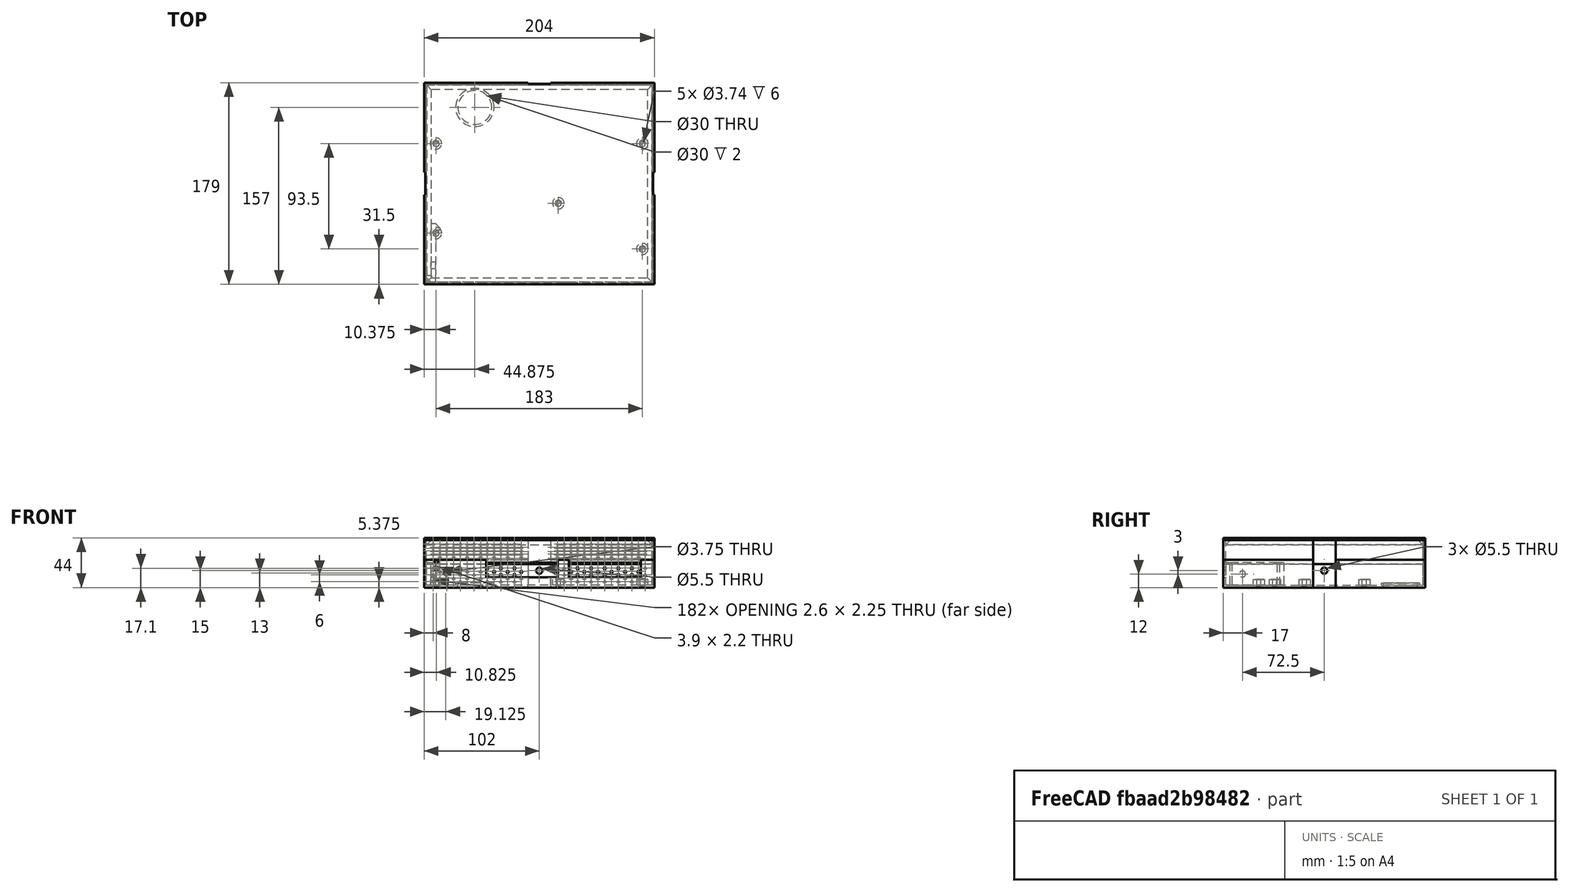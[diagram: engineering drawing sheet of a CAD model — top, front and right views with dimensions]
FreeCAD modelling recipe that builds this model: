
FCSTD DOCUMENT  (FreeCAD 2023.131R26244 +5365 (Git))
Label: Switch
License: All rights reserved
LicenseURL: http://en.wikipedia.org/wiki/All_rights_reserved
objects: Sketcher::SketchObject×26, PartDesign::Pad×13, PartDesign::Pocket×13, PartDesign::Body×4, PartDesign::LinearPattern×3, Spreadsheet::Sheet×1, PartDesign::Fillet×1, PartDesign::Chamfer×1
note: 149 computed .brp shape members not serialized (recipe doc carries the construction recipe); baked Part::Feature solids carry a one-line shape summary decoded from their .brp

FEATURE [Spreadsheet::Sheet] Spreadsheet  label="Parameters"
  PythonMode = false
  ShowCells = 0
  TreeRank = 1
  cells = A1=General; A2=Wall Thickness; B2(Thickness)=2; A3=Width; B3(Width)=200; A4=Depth; B4(Depth)=175; A6=Locking Leaver; B6=This can't be printed; A7=Thickness Multiplier; B7(Locking_Thickness_Multiplier)=2; A8=Lever Width; B8(Locking_Width)=20; A9=Lever Height; B9(Locking_Height)=40; C9=This is the distance between the horizontal locking surfaces, not the entire length of the lever.; A10=Screw Hole Offset; B10(Locking_Hole_Offset)=15; A11=Screw Hole Diameter; B11(Locking_Hole_Diameter)=5.5; A14=Switch Bottom; B14=The origin is the front-left corner, where the reset switch is.; A15=Height; B15(Switch_Bottom_Height)==2 * Switch_LED_Height + Switch_LED_Spacing + Switch_LED_Y; A16=Standoff Mount Height; B16(Switch_Mount_Height)=5.25; A17=Standoff Mount Diameter; B17(Switch_Mount_Diameter)=10.15; A18=Standoff Hole Diameter; B18(Switch_Mount_Hole_Diameter)=3; A19=M3 Nut Diameter; B19(M3_Nut_Diameter)=6.15; A20=M3 Nut Thickness; B20(M3_Nut_Thickness)=2.35; A21=M3 Insert Diameter; B21(M3_Insert_Diameter)=3.74; A22=M3 Insert Length; B22(M3_Insert_Length)=6; A23=Standoff Anchor Type; B23(Switch_Mount_Type)=insert; C23=insert or nut; A24=Mount Offset; B24(Switch_X_Offset)==(Width - 194.25) / 2; C24(Switch_Y_Offset)=0; A25=Front Right Mount; B25(Switch_FR_X)==188.5 + Switch_X_Offset; C25(Switch_FR_Y)==29.5 + Switch_Y_Offset; A26=Front Left Mount; B26(Switch_FL_X)==5.5 + Switch_X_Offset; C26(Switch_FL_Y)==43.5 + Switch_Y_Offset; A27=Middle Mount; B27(Switch_M_X)==114 + Switch_X_Offset; C27(Switch_M_Y)==70 + Switch_Y_Offset; A28=Back Right Mount; B28(Switch_BR_X)==188.5 + Switch_X_Offset; C28(Switch_BR_Y)==123 + Switch_Y_Offset; A29=Back Left Mount; B29(Switch_BL_X)==5.5 + Switch_X_Offset; C29(Switch_BL_Y)==123 + Switch_Y_Offset; A30=RJ45 Block Width; B30(RJ45_Block_Width)=63.55; A31=RJ45 Block Height; B31(RJ45_Block_Height)=13.25; A32=RJ45 Block Spacing; B32(RJ45_Block_Spacing)=10; A33=RJ45 Block Offset; B33(RJ45_Block_X)==50 + Switch_X_Offset; C33(RJ45_Block_Y)==Switch_Mount_Height + 1.75; E33==Switch_Bottom_Height - RJ45_Block_Y - RJ45_Block_Height; A34=Reset Button Diameter; B34(Switch_Reset_Diameter)=3.75; A35=Reset Button Offset; B35(Switch_Reset_X)==14.25 + Switch_X_Offset; C35(Switch_Reset_Y)==Switch_Mount_Height + 5.75; A36=Pass-through Hole Diameter; B36(Switch_Passthrough_Diameter)=30; A37=Pass-through Offset; B37(Switch_Passthrough_X)==40 + Switch_X_Offset; C37(Switch_Passthrough_Y)==155 + Switch_Y_Offset; A38=LED Width; B38(Switch_LED_Width)=3.9; A39=LED Height; B39(Switch_LED_Height)=2.2; A40=LED Spacing; B40(Switch_LED_Spacing)=4.4; A41=LED Offset; B41(Switch_LED_X)==4 + Switch_X_Offset; C41(Switch_LED_Y)==Switch_Mount_Height + 8.75; A42=Air Hole Diameter; B42(Switch_Air_Hole_Diameter)=3; A44=Switch Top; A45=Height; B45(Switch_Top_Height)==40 - Switch_Bottom_Height
FEATURE [Sketcher::SketchObject] Sketch004
  ArcFitTolerance = 1e-06
  AttachmentSupport = -> [XY_Plane001]
  ExternalBSplineMaxDegree = 5
  ExternalBSplineTolerance = 0.0001
  FullyConstrained = true
  InternalTolerance = 1e-06
  InvalidShape = false
  MakeInternals = false
  MapMode = 5
  Support = -> [XY_Plane001]
  TreeRank = 31
  ValidateShape = true
  expr: Constraints[10] = <<Parameters>>.Thickness * <<Parameters>>.Locking_Thickness_Multiplier
  expr: Constraints[11] = <<Parameters>>.Thickness * <<Parameters>>.Locking_Thickness_Multiplier / 2
  expr: Constraints[12] = <<Parameters>>.Thickness * <<Parameters>>.Locking_Thickness_Multiplier
  expr: Constraints[13] = <<Parameters>>.Thickness * <<Parameters>>.Locking_Thickness_Multiplier * 1.5
  expr: Constraints[14] = <<Parameters>>.Thickness * <<Parameters>>.Locking_Thickness_Multiplier
  expr: Constraints[15] = <<Parameters>>.Thickness * <<Parameters>>.Locking_Thickness_Multiplier
  expr: Constraints[33] = <<Parameters>>.Locking_Height
  sketch-geometry (12):
    g0: LineSegment StartX=0 StartY=4 StartZ=0 EndX=4 EndY=0 EndZ=0
    g1: LineSegment StartX=4 StartY=0 StartZ=0 EndX=8 EndY=0 EndZ=0
    g2: LineSegment StartX=8 StartY=0 StartZ=0 EndX=8 EndY=6 EndZ=0
    g3: LineSegment StartX=0 StartY=4 StartZ=0 EndX=0 EndY=6 EndZ=0
    g4: LineSegment StartX=0 StartY=6 StartZ=0 EndX=4 EndY=6 EndZ=0
    g5: LineSegment StartX=4 StartY=46 StartZ=0 EndX=4 EndY=52 EndZ=0
    g6: LineSegment StartX=4 StartY=52 StartZ=0 EndX=8 EndY=52 EndZ=0
    g7: LineSegment StartX=8 StartY=52 StartZ=0 EndX=12 EndY=48 EndZ=0
    g8: LineSegment StartX=12 StartY=48 StartZ=0 EndX=12 EndY=46 EndZ=0
    g9: LineSegment StartX=12 StartY=46 StartZ=0 EndX=8 EndY=46 EndZ=0
    g10: LineSegment StartX=4 StartY=46 StartZ=0 EndX=4 EndY=6 EndZ=0
    g11: LineSegment StartX=8 StartY=46 StartZ=0 EndX=8 EndY=6 EndZ=0
  constraints (36):
    c: PointOnObject(g0,g-2)
    c: PointOnObject(g0,g-1)
    c: Coincident(g1,g0)
    c: PointOnObject(g1,g-1)
    c: Coincident(g2,g1)
    c: Vertical(g2)
    c: Coincident(g3,g0)
    c: PointOnObject(g3,g-2)
    c: Coincident(g4,g3)
    c: Horizontal(g4)
    c: DistanceX(g0,g1) = 4
    c: DistanceY(g0,g3) = 2
    c: DistanceY(g-1,g0) = 4
    c: DistanceY(g-1,g2) = 6
    c: DistanceX(g-1,g0) = 4
    c: DistanceX(g3,g4) = 4
    c: Horizontal(g6)
    c: Coincident(g7,g6)
    c: Coincident(g8,g7)
    c: Vertical(g8)
    c: Coincident(g9,g8)
    c: Horizontal(g9)
    c: Coincident(g6,g5)
    c: Equal(g1,g6)
    c: Equal(g2,g5)
    c: Equal(g0,g7)
    c: Equal(g3,g8)
    c: Equal(g4,g9)
    c: Coincident(g10,g5)
    c: Coincident(g10,g4)
    c: Coincident(g11,g9)
    c: Coincident(g11,g2)
    c: Parallel(g0,g7)
    c: DistanceY(g3,g8) = 40
    c: Vertical(g10)
    c: Vertical(g11)
FEATURE [PartDesign::Pad] Pad003
  AddSubType = 0
  AlongSketchNormal = false
  AutoTaperInnerAngle = true
  CheckUpToFaceLimits = true
  ClaimChildren = false
  Direction = (0,0,1)
  Fit = 0
  FitJoin = 0
  InnerFit = 0
  InnerFitJoin = 0
  InvalidShape = false
  Length = 20
  Length2 = 100
  Linearize = true
  NewSolid = false
  Profile = -> Sketch004
  Suppress = false
  TaperInnerAngle = 0
  TaperInnerAngleRev = 0
  TreeRank = 32
  Type = 0
  ValidateShape = true
  _ProfileBasedVersion = 1
  expr: Length = <<Parameters>>.Locking_Width
FEATURE [Sketcher::SketchObject] Sketch005  label="Bottom Sketch"
  ArcFitTolerance = 1e-06
  AttachmentSupport = -> [XY_Plane]
  ExternalBSplineMaxDegree = 5
  ExternalBSplineTolerance = 0.0001
  FullyConstrained = true
  InternalTolerance = 1e-06
  InvalidShape = false
  MakeInternals = false
  MapMode = 5
  Support = -> [XY_Plane]
  TreeRank = 45
  ValidateShape = true
  expr: Constraints[10] = <<Parameters>>.Width + 2 * <<Parameters>>.Thickness
  expr: Constraints[11] = <<Parameters>>.Depth + 2 * <<Parameters>>.Thickness
  expr: Constraints[12] = <<Parameters>>.Switch_Passthrough_Diameter
  expr: Constraints[13] = <<Parameters>>.Switch_Passthrough_X
  expr: Constraints[14] = <<Parameters>>.Switch_Passthrough_Y
  expr: Constraints[8] = <<Parameters>>.Thickness
  expr: Constraints[9] = <<Parameters>>.Thickness
  sketch-geometry (5):
    g0: LineSegment StartX=-2 StartY=-2 StartZ=0 EndX=202 EndY=-2 EndZ=0
    g1: LineSegment StartX=202 StartY=-2 StartZ=0 EndX=202 EndY=177 EndZ=0
    g2: LineSegment StartX=202 StartY=177 StartZ=0 EndX=-2 EndY=177 EndZ=0
    g3: LineSegment StartX=-2 StartY=177 StartZ=0 EndX=-2 EndY=-2 EndZ=0
    g4: Circle CenterX=42.875 CenterY=155 CenterZ=0 NormalX=0 NormalY=0 NormalZ=1 AngleXU=0 Radius=15
  constraints (15):
    c: Coincident(g0,g1)
    c: Coincident(g1,g2)
    c: Coincident(g2,g3)
    c: Coincident(g3,g0)
    c: Horizontal(g0)
    c: Horizontal(g2)
    c: Vertical(g1)
    c: Vertical(g3)
    c: DistanceX(g0,g-1) = 2
    c: DistanceY(g0,g-1) = 2
    c: DistanceX(g0,g0) = 204
    c: DistanceY(g0,g2) = 179
    c: Diameter(g4) = 30
    c: DistanceX(g-1,g4) = 42.875
    c: DistanceY(g-1,g4) = 155
FEATURE [PartDesign::Pad] Pad  label="Bottom"
  AddSubType = 0
  AlongSketchNormal = false
  AutoTaperInnerAngle = true
  CheckUpToFaceLimits = true
  ClaimChildren = false
  Direction = (0,0,1)
  Fit = 0
  FitJoin = 0
  InnerFit = 0
  InnerFitJoin = 0
  InvalidShape = false
  Length = 2
  Length2 = 100
  Linearize = true
  NewSolid = false
  Profile = -> Sketch005
  Reversed = true
  Suppress = false
  TaperInnerAngle = 0
  TaperInnerAngleRev = 0
  TreeRank = 46
  Type = 0
  ValidateShape = true
  _ProfileBasedVersion = 1
  expr: Length = <<Parameters>>.Thickness
FEATURE [Sketcher::SketchObject] Sketch006  label="Standoff Mounts Drawing"
  ArcFitTolerance = 1e-06
  AttachmentSupport = -> [Pad]
  ExternalBSplineMaxDegree = 5
  ExternalBSplineTolerance = 0.0001
  FullyConstrained = true
  InternalTolerance = 1e-06
  InvalidShape = false
  MakeInternals = false
  MapMode = 5
  Support = -> [Pad]
  TreeRank = 47
  ValidateShape = true
  expr: Constraints[0] = <<Parameters>>.Switch_Mount_Diameter
  expr: Constraints[11] = <<Parameters>>.Switch_BR_X
  expr: Constraints[12] = <<Parameters>>.Switch_BR_Y
  expr: Constraints[13] = <<Parameters>>.Switch_BL_X
  expr: Constraints[14] = <<Parameters>>.Switch_BL_Y
  expr: Constraints[16] = <<Parameters>>.Switch_Mount_Hole_Diameter
  expr: Constraints[1] = <<Parameters>>.Switch_FR_X
  expr: Constraints[2] = <<Parameters>>.Switch_FR_Y
  expr: Constraints[4] = <<Parameters>>.Switch_FL_Y
  expr: Constraints[5] = <<Parameters>>.Switch_FL_X
  expr: Constraints[7] = <<Parameters>>.Switch_M_X
  expr: Constraints[8] = <<Parameters>>.Switch_M_Y
  sketch-geometry (10):
    g0: Circle CenterX=191.375 CenterY=29.5 CenterZ=0 NormalX=0 NormalY=0 NormalZ=1 AngleXU=0 Radius=5.075
    g1: Circle CenterX=8.375 CenterY=43.5 CenterZ=0 NormalX=0 NormalY=0 NormalZ=1 AngleXU=0 Radius=5.075
    g2: Circle CenterX=116.875 CenterY=70 CenterZ=0 NormalX=0 NormalY=0 NormalZ=1 AngleXU=0 Radius=5.075
    g3: Circle CenterX=191.375 CenterY=123 CenterZ=0 NormalX=0 NormalY=0 NormalZ=1 AngleXU=0 Radius=5.075
    g4: Circle CenterX=8.375 CenterY=123 CenterZ=0 NormalX=0 NormalY=0 NormalZ=1 AngleXU=0 Radius=5.075
    g5: Circle CenterX=191.375 CenterY=29.5 CenterZ=0 NormalX=0 NormalY=0 NormalZ=1 AngleXU=0 Radius=1.5
    g6: Circle CenterX=116.875 CenterY=70 CenterZ=0 NormalX=0 NormalY=0 NormalZ=1 AngleXU=0 Radius=1.5
    g7: Circle CenterX=191.375 CenterY=123 CenterZ=0 NormalX=0 NormalY=0 NormalZ=1 AngleXU=0 Radius=1.5
    g8: Circle CenterX=8.375 CenterY=43.5 CenterZ=0 NormalX=0 NormalY=0 NormalZ=1 AngleXU=0 Radius=1.5
    g9: Circle CenterX=8.375 CenterY=123 CenterZ=0 NormalX=0 NormalY=0 NormalZ=1 AngleXU=0 Radius=1.5
  constraints (25):
    c: Diameter(g0) = 10.15
    c: DistanceX(g-1,g0) = 191.375
    c: DistanceY(g-1,g0) = 29.5
    c: Equal(g0,g1)
    c: DistanceY(g-1,g1) = 43.5
    c: DistanceX(g-1,g1) = 8.375
    c: Equal(g0,g2)
    c: DistanceX(g-1,g2) = 116.875
    c: DistanceY(g-1,g2) = 70
    c: Equal(g0,g3)
    c: Equal(g0,g4)
    c: DistanceX(g-1,g3) = 191.375
    c: DistanceY(g-1,g3) = 123
    c: DistanceX(g-1,g4) = 8.375
    c: DistanceY(g-1,g4) = 123
    c: Coincident(g5,g0)
    c: Diameter(g5) = 3
    c: Coincident(g6,g2)
    c: Coincident(g7,g3)
    c: Coincident(g8,g1)
    c: Coincident(g9,g4)
    c: Equal(g5,g6)
    c: Equal(g5,g8)
    c: Equal(g5,g7)
    c: Equal(g5,g9)
FEATURE [PartDesign::Pad] Pad004  label="Standoff Mounts"
  AddSubType = 0
  AlongSketchNormal = false
  AutoTaperInnerAngle = true
  BaseFeature = -> Pad
  CheckUpToFaceLimits = true
  ClaimChildren = false
  Direction = (0,0,1)
  Fit = 0
  FitJoin = 0
  InnerFit = 0
  InnerFitJoin = 0
  InvalidShape = false
  Length = 5.25
  Length2 = 100
  Linearize = true
  NewSolid = false
  Profile = -> Sketch006
  Suppress = false
  TaperInnerAngle = 0
  TaperInnerAngleRev = 0
  TreeRank = 48
  Type = 0
  ValidateShape = true
  _ProfileBasedVersion = 1
  expr: Length = <<Parameters>>.Switch_Mount_Height
FEATURE [Sketcher::SketchObject] Sketch007  label="Nut Holes Sketch"
  ArcFitTolerance = 1e-06
  AttachmentSupport = -> [Pad004]
  ExternalBSplineMaxDegree = 5
  ExternalBSplineTolerance = 0.0001
  FullyConstrained = false
  InternalTolerance = 1e-06
  InvalidShape = false
  MakeInternals = false
  MapMode = 5
  Placement = pos=(0,0,5.25) rot=(0,0,1;0rad)
  Support = -> [Pad004]
  TreeRank = 49
  ValidateShape = true
  expr: Constraints[17] = <<Parameters>>.M3_Nut_Diameter
  expr: Constraints[18] = <<Parameters>>.Switch_FR_X
  expr: Constraints[19] = <<Parameters>>.Switch_FR_Y
  expr: Constraints[74] = <<Parameters>>.Switch_M_X
  expr: Constraints[75] = <<Parameters>>.Switch_M_Y
  expr: Constraints[76] = <<Parameters>>.Switch_FL_X
  expr: Constraints[77] = <<Parameters>>.Switch_FL_Y
  expr: Constraints[78] = <<Parameters>>.Switch_BL_X
  expr: Constraints[79] = <<Parameters>>.Switch_BL_Y
  expr: Constraints[98] = <<Parameters>>.Switch_BR_X
  expr: Constraints[99] = <<Parameters>>.Switch_BR_Y
  sketch-geometry (35):
    g0: LineSegment StartX=188.799 StartY=31.1785 StartZ=0 EndX=188.633 EndY=28.108 EndZ=0
    g1: LineSegment StartX=188.633 StartY=28.108 StartZ=0 EndX=191.21 EndY=26.4295 EndZ=0
    g2: LineSegment StartX=191.21 StartY=26.4295 StartZ=0 EndX=193.951 EndY=27.8215 EndZ=0
    g3: LineSegment StartX=193.951 StartY=27.8215 StartZ=0 EndX=194.117 EndY=30.892 EndZ=0
    g4: LineSegment StartX=194.117 StartY=30.892 StartZ=0 EndX=191.54 EndY=32.5705 EndZ=0
    g5: LineSegment StartX=191.54 StartY=32.5705 StartZ=0 EndX=188.799 EndY=31.1785 EndZ=0
    g6: Circle [constr] CenterX=191.375 CenterY=29.5 CenterZ=0 NormalX=0 NormalY=0 NormalZ=1 AngleXU=0 Radius=3.075
    g7: LineSegment StartX=117.133 StartY=73.0641 StartZ=0 EndX=114.351 EndY=71.7559 EndZ=0
    g8: LineSegment StartX=114.351 StartY=71.7559 StartZ=0 EndX=114.092 EndY=68.6917 EndZ=0
    g9: LineSegment StartX=114.092 StartY=68.6917 StartZ=0 EndX=116.617 EndY=66.9359 EndZ=0
    g10: LineSegment StartX=116.617 StartY=66.9359 StartZ=0 EndX=119.399 EndY=68.2441 EndZ=0
    g11: LineSegment StartX=119.399 StartY=68.2441 StartZ=0 EndX=119.658 EndY=71.3083 EndZ=0
    g12: LineSegment StartX=119.658 StartY=71.3083 StartZ=0 EndX=117.133 EndY=73.0641 EndZ=0
    g13: Circle [constr] CenterX=116.875 CenterY=70 CenterZ=0 NormalX=0 NormalY=0 NormalZ=1 AngleXU=0 Radius=3.075
    g14: LineSegment StartX=10.9135 StartY=45.2354 StartZ=0 EndX=8.14135 EndY=46.5661 EndZ=0
    g15: LineSegment StartX=8.14135 StartY=46.5661 StartZ=0 EndX=5.60285 EndY=44.8307 EndZ=0
    g16: LineSegment StartX=5.60285 StartY=44.8307 StartZ=0 EndX=5.83649 EndY=41.7646 EndZ=0
    g17: LineSegment StartX=5.83649 StartY=41.7646 StartZ=0 EndX=8.60865 EndY=40.4339 EndZ=0
    g18: LineSegment StartX=8.60865 StartY=40.4339 StartZ=0 EndX=11.1472 EndY=42.1693 EndZ=0
    g19: LineSegment StartX=11.1472 StartY=42.1693 StartZ=0 EndX=10.9135 EndY=45.2354 EndZ=0
    g20: Circle [constr] CenterX=8.375 CenterY=43.5 CenterZ=0 NormalX=0 NormalY=0 NormalZ=1 AngleXU=0 Radius=3.075
    g21: LineSegment StartX=10.8456 StartY=124.831 StartZ=0 EndX=8.0248 EndY=126.055 EndZ=0
    g22: LineSegment StartX=8.0248 StartY=126.055 StartZ=0 EndX=5.5542 EndY=124.224 EndZ=0
    g23: LineSegment StartX=5.5542 StartY=124.224 StartZ=0 EndX=5.9044 EndY=121.169 EndZ=0
    g24: LineSegment StartX=5.9044 StartY=121.169 StartZ=0 EndX=8.7252 EndY=119.945 EndZ=0
    g25: LineSegment StartX=8.7252 StartY=119.945 StartZ=0 EndX=11.1958 EndY=121.776 EndZ=0
    g26: LineSegment StartX=11.1958 StartY=121.776 StartZ=0 EndX=10.8456 EndY=124.831 EndZ=0
    g27: Circle [constr] CenterX=8.375 CenterY=123 CenterZ=0 NormalX=0 NormalY=0 NormalZ=1 AngleXU=0 Radius=3.075
    g28: LineSegment StartX=188.744 StartY=124.591 StartZ=0 EndX=188.681 EndY=121.517 EndZ=0
    g29: LineSegment StartX=188.681 StartY=121.517 StartZ=0 EndX=191.313 EndY=119.926 EndZ=0
    g30: LineSegment StartX=191.313 StartY=119.926 StartZ=0 EndX=194.006 EndY=121.409 EndZ=0
    g31: LineSegment StartX=194.006 StartY=121.409 StartZ=0 EndX=194.069 EndY=124.483 EndZ=0
    g32: LineSegment StartX=194.069 StartY=124.483 StartZ=0 EndX=191.437 EndY=126.074 EndZ=0
    g33: LineSegment StartX=191.437 StartY=126.074 StartZ=0 EndX=188.744 EndY=124.591 EndZ=0
    g34: Circle [constr] CenterX=191.375 CenterY=123 CenterZ=0 NormalX=0 NormalY=0 NormalZ=1 AngleXU=0 Radius=3.075
  constraints (80):
    c: Coincident(g0,g1)
    c: Coincident(g1,g2)
    c: Coincident(g2,g3)
    c: Coincident(g3,g4)
    c: Coincident(g4,g5)
    c: Coincident(g5,g0)
    c: Equal(g0, g1-g5) x5
    c: PointOnObject(g0,g6)
    c: PointOnObject(g1,g6)
    c: PointOnObject(g2,g6)
    c: PointOnObject(g3,g6)
    c: PointOnObject(g4,g6)
    c: PointOnObject(g5,g6)
    c: Diameter(g6) = 6.15
    c: DistanceX(g-1,g6) = 191.375
    c: DistanceY(g-1,g6) = 29.5
    c: Coincident(g7,g8)
    c: Coincident(g8,g9)
    c: Coincident(g9,g10)
    c: Coincident(g10,g11)
    c: Coincident(g11,g12)
    c: Coincident(g12,g7)
    c: Equal(g7, g8-g12) x5
    c: PointOnObject(g7,g13)
    c: PointOnObject(g8,g13)
    c: PointOnObject(g9,g13)
    c: PointOnObject(g10,g13)
    c: PointOnObject(g11,g13)
    c: PointOnObject(g12,g13)
    c: Coincident(g14,g15)
    c: Coincident(g15,g16)
    c: Coincident(g16,g17)
    c: Coincident(g17,g18)
    c: Coincident(g18,g19)
    c: Coincident(g19,g14)
    c: Equal(g14, g15-g19) x5
    c: PointOnObject(g14,g20)
    c: PointOnObject(g15,g20)
    c: PointOnObject(g16,g20)
    c: PointOnObject(g17,g20)
    c: PointOnObject(g18,g20)
    c: PointOnObject(g19,g20)
    c: Coincident(g21,g22)
    c: Coincident(g22,g23)
    c: Coincident(g23,g24)
    c: Coincident(g24,g25)
    c: Coincident(g25,g26)
    c: Coincident(g26,g21)
    c: Equal(g21, g22-g26) x5
    c: PointOnObject(g21,g27)
    c: PointOnObject(g22,g27)
    c: PointOnObject(g23,g27)
    c: PointOnObject(g24,g27)
    c: PointOnObject(g25,g27)
    c: PointOnObject(g26,g27)
    c: Equal(g6,g13)
    c: Equal(g6,g20)
    c: Equal(g6,g27)
    c: DistanceX(g-1,g13) = 116.875
    c: DistanceY(g-1,g13) = 70
    c: DistanceX(g-1,g20) = 8.375
    c: DistanceY(g-1,g20) = 43.5
    c: DistanceX(g-1,g27) = 8.375
    c: DistanceY(g-1,g27) = 123
    c: Coincident(g28,g29)
    c: Coincident(g29,g30)
    c: Coincident(g30,g31)
    c: Coincident(g31,g32)
    c: Coincident(g32,g33)
    c: Coincident(g33,g28)
    c: Equal(g28, g29-g33) x5
    c: PointOnObject(g28,g34)
    c: PointOnObject(g29,g34)
    c: PointOnObject(g30,g34)
    c: PointOnObject(g31,g34)
    c: PointOnObject(g32,g34)
    c: PointOnObject(g33,g34)
    c: Equal(g6,g34)
    c: DistanceX(g-1,g34) = 191.375
    c: DistanceY(g-1,g34) = 123
FEATURE [PartDesign::Pocket] Pocket  label="Nut Holes"
  AddSubType = 1
  AutoTaperInnerAngle = true
  BaseFeature = -> Pad004
  CheckUpToFaceLimits = true
  ClaimChildren = false
  Fit = 0
  FitJoin = 0
  InnerFit = 0
  InnerFitJoin = 0
  InvalidShape = false
  Length = 0.0001
  Length2 = 100
  Linearize = true
  NewSolid = false
  Profile = -> Sketch007
  Suppress = false
  TaperInnerAngle = 0
  TaperInnerAngleRev = 0
  TreeRank = 50
  Type = 0
  ValidateShape = true
  _ProfileBasedVersion = 1
  _Version = 1
  expr: Length = <<Parameters>>.Switch_Mount_Type == <<nut>> ? <<Parameters>>.M3_Nut_Thickness : 0.0001
FEATURE [Sketcher::SketchObject] Sketch008  label="Walls Sketch"
  ArcFitTolerance = 1e-06
  AttachmentSupport = -> [Pocket]
  ExternalBSplineMaxDegree = 5
  ExternalBSplineTolerance = 0.0001
  FullyConstrained = true
  InternalTolerance = 1e-06
  InvalidShape = false
  MakeInternals = false
  MapMode = 5
  Support = -> [Pocket]
  TreeRank = 51
  ValidateShape = true
  expr: Constraints[10] = <<Parameters>>.Width + 2 * <<Parameters>>.Thickness
  expr: Constraints[11] = <<Parameters>>.Depth + 2 * <<Parameters>>.Thickness
  expr: Constraints[20] = <<Parameters>>.Thickness
  expr: Constraints[21] = <<Parameters>>.Thickness
  expr: Constraints[22] = <<Parameters>>.Width
  expr: Constraints[23] = <<Parameters>>.Depth
  expr: Constraints[8] = <<Parameters>>.Thickness
  expr: Constraints[9] = <<Parameters>>.Thickness
  sketch-geometry (8):
    g0: LineSegment StartX=-2 StartY=-2 StartZ=0 EndX=202 EndY=-2 EndZ=0
    g1: LineSegment StartX=202 StartY=-2 StartZ=0 EndX=202 EndY=177 EndZ=0
    g2: LineSegment StartX=202 StartY=177 StartZ=0 EndX=-2 EndY=177 EndZ=0
    g3: LineSegment StartX=-2 StartY=177 StartZ=0 EndX=-2 EndY=-2 EndZ=0
    g4: LineSegment StartX=1e-16 StartY=175 StartZ=0 EndX=200 EndY=175 EndZ=0
    g5: LineSegment StartX=200 StartY=175 StartZ=0 EndX=200 EndY=0 EndZ=0
    g6: LineSegment StartX=200 StartY=1e-16 StartZ=0 EndX=0 EndY=1e-16 EndZ=0
    g7: LineSegment StartX=1e-16 StartY=1e-16 StartZ=0 EndX=1e-16 EndY=175 EndZ=0
  constraints (24):
    c: Coincident(g0,g1)
    c: Coincident(g1,g2)
    c: Coincident(g2,g3)
    c: Coincident(g3,g0)
    c: Horizontal(g0)
    c: Horizontal(g2)
    c: Vertical(g1)
    c: Vertical(g3)
    c: DistanceY(g0,g-1) = 2
    c: DistanceX(g0,g-1) = 2
    c: DistanceX(g0,g0) = 204
    c: DistanceY(g0,g2) = 179
    c: Coincident(g4,g5)
    c: Coincident(g5,g6)
    c: Coincident(g6,g7)
    c: Coincident(g7,g4)
    c: Horizontal(g4)
    c: Horizontal(g6)
    c: Vertical(g5)
    c: Vertical(g7)
    c: DistanceX(g0,g6) = 2
    c: DistanceY(g0,g6) = 2
    c: DistanceX(g4,g4) = 200
    c: DistanceY(g5,g4) = 175
FEATURE [Sketcher::SketchObject] Sketch011  label="Passthrough Support Sketch"
  ArcFitTolerance = 1e-06
  ExternalBSplineMaxDegree = 5
  ExternalBSplineTolerance = 0.0001
  FullyConstrained = true
  InternalTolerance = 1e-06
  InvalidShape = false
  MakeInternals = false
  MapMode = 5
  TreeRank = 57
  ValidateShape = true
  expr: Constraints[1] = <<Parameters>>.Switch_Passthrough_Diameter
  expr: Constraints[2] = <<Parameters>>.Switch_Passthrough_Diameter + 2 * <<Parameters>>.Thickness
  expr: Constraints[3] = <<Parameters>>.Switch_Passthrough_X
  expr: Constraints[4] = <<Parameters>>.Switch_Passthrough_Y
  sketch-geometry (2):
    g0: Circle CenterX=42.875 CenterY=155 CenterZ=0 NormalX=0 NormalY=0 NormalZ=1 AngleXU=0 Radius=17
    g1: Circle CenterX=42.875 CenterY=155 CenterZ=0 NormalX=0 NormalY=0 NormalZ=1 AngleXU=0 Radius=15
  constraints (5):
    c: Coincident(g1,g0)
    c: Diameter(g1) = 30
    c: Diameter(g0) = 34
    c: DistanceX(g-1,g0) = 42.875
    c: DistanceY(g-1,g0) = 155
FEATURE [Sketcher::SketchObject] Sketch
  ArcFitTolerance = 1e-06
  AttachmentSupport = -> [Pad003]
  ExternalBSplineMaxDegree = 5
  ExternalBSplineTolerance = 0.0001
  FullyConstrained = true
  InternalTolerance = 1e-06
  InvalidShape = false
  MakeInternals = false
  MapMode = 5
  Placement = pos=(4,0,0) rot=(0.57735,-0.57735,-0.57735;2.0944rad)
  Support = -> [Pad003]
  TreeRank = 62
  ValidateShape = true
  expr: Constraints[0] = <<Parameters>>.Locking_Hole_Diameter
  expr: Constraints[1] = <<Parameters>>.Locking_Width / 2
  expr: Constraints[2] = <<Parameters>>.Locking_Hole_Offset
  sketch-geometry (1):
    g0: Circle CenterX=-15 CenterY=10 CenterZ=0 NormalX=0 NormalY=0 NormalZ=1 AngleXU=0 Radius=2.75
  constraints (3):
    c: Diameter(g0) = 5.5
    c: DistanceY(g-1,g0) = 10
    c: DistanceX(g0,g-1) = 15
FEATURE [PartDesign::Pocket] Pocket004
  AddSubType = 1
  AutoTaperInnerAngle = true
  BaseFeature = -> Pad003
  CheckUpToFaceLimits = true
  ClaimChildren = false
  Fit = 0
  FitJoin = 0
  InnerFit = 0
  InnerFitJoin = 0
  InvalidShape = false
  Length = 4
  Length2 = 100
  Linearize = true
  NewSolid = false
  Profile = -> Sketch
  Suppress = false
  TaperInnerAngle = 0
  TaperInnerAngleRev = 0
  TreeRank = 63
  Type = 0
  ValidateShape = true
  _ProfileBasedVersion = 1
  _Version = 1
  expr: Length = <<Parameters>>.Locking_Thickness_Multiplier * <<Parameters>>.Thickness
FEATURE [PartDesign::Fillet] Fillet
  AddSubType = 0
  Base = -> Pocket004 [Edge3,Edge8,Edge6,Edge7,Edge2,Edge29,Edge19,Edge9,Edge28,Edge18,Edge20,Edge10]
  BaseFeature = -> Pocket004
  InvalidShape = false
  NewSolid = false
  Radius = 1
  SupportTransform = false
  Suppress = false
  TreeRank = 66
  ValidateShape = true
FEATURE [PartDesign::Body] Body001  label="Locking Lever"
  AutoGroupSolids = false
  ClaimAllChildren = false
  ExportMode = 0
  Group = -> [Sketch004,Pad003,Sketch,Pocket004,Fillet]
  InvalidShape = false
  Origin = -> Origin001
  Tip = -> Fillet
  TreeRank = 30
  ValidateShape = true
  _ExportChildren = -> [Pad003,Pocket004,Fillet]
  _GroupVersion = 1
FEATURE [Sketcher::SketchObject] Sketch018  label="Switch Top Walls Sketch"
  ArcFitTolerance = 1e-06
  AttachmentOffset = pos=(0,0,22.8) rot=(0,0,1;0rad)
  AttachmentSupport = -> [XY_Plane002]
  ExternalBSplineMaxDegree = 5
  ExternalBSplineTolerance = 0.0001
  FullyConstrained = true
  InternalTolerance = 1e-06
  InvalidShape = false
  MakeInternals = false
  MapMode = 5
  Placement = pos=(0,0,22.8) rot=(0,0,1;0rad)
  Support = -> [XY_Plane002]
  TreeRank = 88
  ValidateShape = true
  expr: AttachmentOffset.Base.z = <<Parameters>>.Switch_Bottom_Height
  expr: Constraints[10] = <<Parameters>>.Thickness
  expr: Constraints[11] = <<Parameters>>.Thickness
  expr: Constraints[20] = <<Parameters>>.Width
  expr: Constraints[21] = <<Parameters>>.Depth
  expr: Constraints[8] = <<Parameters>>.Width + 2 * <<Parameters>>.Thickness
  expr: Constraints[9] = <<Parameters>>.Depth + 2 * <<Parameters>>.Thickness
  sketch-geometry (8):
    g0: LineSegment StartX=-2 StartY=177 StartZ=0 EndX=202 EndY=177 EndZ=0
    g1: LineSegment StartX=202 StartY=177 StartZ=0 EndX=202 EndY=-2 EndZ=0
    g2: LineSegment StartX=202 StartY=-2 StartZ=0 EndX=-2 EndY=-2 EndZ=0
    g3: LineSegment StartX=-2 StartY=-2 StartZ=0 EndX=-2 EndY=177 EndZ=0
    g4: LineSegment StartX=0 StartY=175 StartZ=0 EndX=200 EndY=175 EndZ=0
    g5: LineSegment StartX=200 StartY=175 StartZ=0 EndX=200 EndY=0 EndZ=0
    g6: LineSegment StartX=200 StartY=0 StartZ=0 EndX=0 EndY=0 EndZ=0
    g7: LineSegment StartX=0 StartY=0 StartZ=0 EndX=0 EndY=175 EndZ=0
  constraints (23):
    c: Coincident(g0,g1)
    c: Coincident(g1,g2)
    c: Coincident(g2,g3)
    c: Coincident(g3,g0)
    c: Horizontal(g0)
    c: Horizontal(g2)
    c: Vertical(g1)
    c: Vertical(g3)
    c: DistanceX(g2,g1) = 204
    c: DistanceY(g2,g0) = 179
    c: DistanceY(g2,g-1) = 2
    c: DistanceX(g2,g-1) = 2
    c: Coincident(g4,g5)
    c: Coincident(g5,g6)
    c: Coincident(g6,g7)
    c: Coincident(g7,g4)
    c: Horizontal(g4)
    c: Horizontal(g6)
    c: Vertical(g5)
    c: Vertical(g7)
    c: DistanceX(g6,g5) = 200
    c: DistanceY(g6,g4) = 175
    c: Coincident(g6,g-1)
FEATURE [PartDesign::Pad] Pad007  label="Switch Top Walls"
  AddSubType = 0
  AlongSketchNormal = false
  AutoTaperInnerAngle = true
  CheckUpToFaceLimits = true
  ClaimChildren = false
  Direction = (0,0,1)
  Fit = 0
  FitJoin = 0
  InnerFit = 0
  InnerFitJoin = 0
  InvalidShape = false
  Length = 17.2
  Length2 = 100
  Linearize = true
  NewSolid = false
  Profile = -> Sketch018
  Suppress = false
  TaperInnerAngle = 0
  TaperInnerAngleRev = 0
  TreeRank = 89
  Type = 0
  ValidateShape = true
  _ProfileBasedVersion = 1
  expr: Length = <<Parameters>>.Switch_Top_Height
FEATURE [Sketcher::SketchObject] Sketch019  label="Switch Top Top Sketch"
  ArcFitTolerance = 1e-06
  AttachmentSupport = -> [Pad007]
  ExternalBSplineMaxDegree = 5
  ExternalBSplineTolerance = 0.0001
  FullyConstrained = true
  InternalTolerance = 1e-06
  InvalidShape = false
  MakeInternals = false
  MapMode = 5
  Placement = pos=(0,0,40) rot=(0,0,1;0rad)
  Support = -> [Pad007]
  TreeRank = 90
  ValidateShape = true
  expr: Constraints[10] = <<Parameters>>.Thickness
  expr: Constraints[11] = <<Parameters>>.Thickness
  expr: Constraints[8] = <<Parameters>>.Width + 2 * <<Parameters>>.Thickness
  expr: Constraints[9] = <<Parameters>>.Depth + 2 * <<Parameters>>.Thickness
  sketch-geometry (4):
    g0: LineSegment StartX=-2 StartY=177 StartZ=0 EndX=202 EndY=177 EndZ=0
    g1: LineSegment StartX=202 StartY=177 StartZ=0 EndX=202 EndY=-2 EndZ=0
    g2: LineSegment StartX=202 StartY=-2 StartZ=0 EndX=-2 EndY=-2 EndZ=0
    g3: LineSegment StartX=-2 StartY=-2 StartZ=0 EndX=-2 EndY=177 EndZ=0
  constraints (12):
    c: Coincident(g0,g1)
    c: Coincident(g1,g2)
    c: Coincident(g2,g3)
    c: Coincident(g3,g0)
    c: Horizontal(g0)
    c: Horizontal(g2)
    c: Vertical(g1)
    c: Vertical(g3)
    c: DistanceX(g2,g1) = 204
    c: DistanceY(g1,g0) = 179
    c: DistanceX(g2,g-1) = 2
    c: DistanceY(g2,g-1) = 2
FEATURE [PartDesign::Pad] Pad008  label="Switch Top Top"
  AddSubType = 0
  AlongSketchNormal = false
  AutoTaperInnerAngle = true
  BaseFeature = -> Pad007
  CheckUpToFaceLimits = true
  ClaimChildren = false
  Direction = (0,0,1)
  Fit = 0
  FitJoin = 0
  InnerFit = 0
  InnerFitJoin = 0
  InvalidShape = false
  Length = 2
  Length2 = 100
  Linearize = true
  NewSolid = false
  Profile = -> Sketch019
  Suppress = false
  TaperInnerAngle = 0
  TaperInnerAngleRev = 0
  TreeRank = 91
  Type = 0
  ValidateShape = true
  _ProfileBasedVersion = 1
  expr: Length = <<Parameters>>.Thickness
FEATURE [Sketcher::SketchObject] Sketch020  label="Switch Top Wall Recess Sketch"
  ArcFitTolerance = 1e-06
  AttachmentSupport = -> [Pad008]
  ExternalBSplineMaxDegree = 5
  ExternalBSplineTolerance = 0.0001
  FullyConstrained = true
  InternalTolerance = 1e-06
  InvalidShape = false
  MakeInternals = false
  MapMode = 5
  Placement = pos=(0,0,22.8) rot=(1,0,0;3.14159rad)
  Support = -> [Pad008]
  TreeRank = 92
  ValidateShape = true
  expr: Constraints[10] = <<Parameters>>.Thickness / 2
  expr: Constraints[11] = <<Parameters>>.Thickness / 2
  expr: Constraints[21] = <<Parameters>>.Width
  expr: Constraints[22] = <<Parameters>>.Depth
  expr: Constraints[24] = <<Parameters>>.RJ45_Block_X
  expr: Constraints[26] = <<Parameters>>.RJ45_Block_Width
  expr: Constraints[30] = <<Parameters>>.RJ45_Block_Spacing
  expr: Constraints[34] = <<Parameters>>.RJ45_Block_Width
  expr: Constraints[49] = <<Parameters>>.Switch_LED_Width
  expr: Constraints[50] = <<Parameters>>.Switch_LED_X
  expr: Constraints[8] = <<Parameters>>.Width + <<Parameters>>.Thickness
  expr: Constraints[9] = <<Parameters>>.Depth + <<Parameters>>.Thickness
  sketch-geometry (20):
    g0: LineSegment StartX=-1 StartY=1 StartZ=0 EndX=6.875 EndY=1 EndZ=0
    g1: LineSegment StartX=201 StartY=1 StartZ=0 EndX=201 EndY=-176 EndZ=0
    g2: LineSegment StartX=201 StartY=-176 StartZ=0 EndX=-1 EndY=-176 EndZ=0
    g3: LineSegment StartX=-1 StartY=-176 StartZ=0 EndX=-1 EndY=1 EndZ=0
    g4: LineSegment StartX=0 StartY=0 StartZ=0 EndX=6.875 EndY=0 EndZ=0
    g5: LineSegment StartX=200 StartY=0 StartZ=0 EndX=200 EndY=-175 EndZ=0
    g6: LineSegment StartX=200 StartY=-175 StartZ=0 EndX=0 EndY=-175 EndZ=0
    g7: LineSegment StartX=0 StartY=-175 StartZ=0 EndX=0 EndY=0 EndZ=0
    g8: LineSegment StartX=52.875 StartY=1 StartZ=0 EndX=52.875 EndY=0 EndZ=0
    g9: LineSegment StartX=116.425 StartY=1 StartZ=0 EndX=116.425 EndY=0 EndZ=0
    g10: LineSegment StartX=126.425 StartY=1 StartZ=0 EndX=126.425 EndY=0 EndZ=0
    g11: LineSegment StartX=189.975 StartY=1 StartZ=0 EndX=189.975 EndY=0 EndZ=0
    g12: LineSegment StartX=116.425 StartY=0 StartZ=0 EndX=126.425 EndY=0 EndZ=0
    g13: LineSegment StartX=116.425 StartY=1 StartZ=0 EndX=126.425 EndY=1 EndZ=0
    g14: LineSegment StartX=189.975 StartY=0 StartZ=0 EndX=200 EndY=0 EndZ=0
    g15: LineSegment StartX=189.975 StartY=1 StartZ=0 EndX=201 EndY=1 EndZ=0
    g16: LineSegment StartX=6.875 StartY=1 StartZ=0 EndX=6.875 EndY=0 EndZ=0
    g17: LineSegment StartX=10.775 StartY=1 StartZ=0 EndX=10.775 EndY=0 EndZ=0
    g18: LineSegment StartX=10.775 StartY=0 StartZ=0 EndX=52.875 EndY=0 EndZ=0
    g19: LineSegment StartX=10.775 StartY=1 StartZ=0 EndX=52.875 EndY=1 EndZ=0
  constraints (59):
    c: Coincident(g15,g1)
    c: Coincident(g1,g2)
    c: Coincident(g2,g3)
    c: Coincident(g3,g0)
    c: Horizontal(g0)
    c: Horizontal(g2)
    c: Vertical(g1)
    c: Vertical(g3)
    c: DistanceX(g2,g1) = 202
    c: DistanceY(g1,g15) = 177
    c: DistanceY(g-1,g0) = 1
    c: DistanceX(g0,g-1) = 1
    c: Coincident(g14,g5)
    c: Coincident(g5,g6)
    c: Coincident(g6,g7)
    c: Coincident(g7,g4)
    c: Horizontal(g4)
    c: Horizontal(g6)
    c: Vertical(g5)
    c: Vertical(g7)
    c: Coincident(g4,g-1)
    c: DistanceX(g4,g14) = 200
    c: DistanceY(g6,g4) = 175
    c: Vertical(g8)
    c: DistanceX(g4,g8) = 52.875
    c: Vertical(g9)
    c: DistanceX(g8,g9) = 63.55
    c: PointOnObject(g10,g0)
    c: PointOnObject(g10,g4)
    c: Vertical(g10)
    c: DistanceX(g9,g10) = 10
    c: PointOnObject(g11,g0)
    c: PointOnObject(g11,g4)
    c: Vertical(g11)
    c: DistanceX(g10,g11) = 63.55
    c: Coincident(g18,g8)
    c: Coincident(g12,g9)
    c: Coincident(g19,g8)
    c: Coincident(g13,g9)
    c: Coincident(g13,g10)
    c: Coincident(g12,g10)
    c: Horizontal(g13)
    c: Horizontal(g12)
    c: Horizontal(g15)
    c: Horizontal(g14)
    c: Coincident(g11,g15)
    c: Coincident(g14,g11)
    c: Vertical(g17)
    c: Vertical(g16)
    c: DistanceX(g16,g17) = 3.9
    c: DistanceX(g4,g16) = 6.875
    c: Coincident(g4,g16)
    c: Coincident(g18,g17)
    c: Coincident(g0,g16)
    c: Coincident(g19,g17)
    c: Horizontal(g19)
    c: Horizontal(g18)
    c: PointOnObject(g17,g-1)
    c: Equal(g16,g17)
FEATURE [PartDesign::Pad] Pad009  label="Switch Top Wall Recess"
  AddSubType = 0
  AlongSketchNormal = false
  AutoTaperInnerAngle = true
  BaseFeature = -> Pad008
  CheckUpToFaceLimits = true
  ClaimChildren = false
  Direction = (0,0,-1)
  Fit = 0
  FitJoin = 0
  InnerFit = 0
  InnerFitJoin = 0
  InvalidShape = false
  Length = 4
  Length2 = 100
  Linearize = true
  NewSolid = false
  Profile = -> Sketch020
  Suppress = false
  TaperInnerAngle = 0
  TaperInnerAngleRev = 0
  TreeRank = 93
  Type = 0
  ValidateShape = true
  _ProfileBasedVersion = 1
  expr: Length = <<Parameters>>.Thickness * 2
FEATURE [Sketcher::SketchObject] Sketch021  label="Switch Top Lock Relief Sketch"
  ArcFitTolerance = 1e-06
  AttachmentSupport = -> [Pad009]
  ExternalBSplineMaxDegree = 5
  ExternalBSplineTolerance = 0.0001
  FullyConstrained = true
  InternalTolerance = 1e-06
  InvalidShape = false
  MakeInternals = false
  MapMode = 5
  Placement = pos=(0,0,42) rot=(0,0,1;0rad)
  Support = -> [Pad009]
  TreeRank = 94
  ValidateShape = true
  expr: Constraints[27] = <<Parameters>>.Locking_Width
  expr: Constraints[30] = <<Parameters>>.Thickness / 2
  expr: Constraints[33] = <<Parameters>>.Thickness / 2
  expr: Constraints[34] = <<Parameters>>.Width + <<Parameters>>.Thickness / 2
  expr: Constraints[35] = <<Parameters>>.Depth / 2
  expr: Constraints[36] = <<Parameters>>.Depth / 2
  expr: Constraints[37] = <<Parameters>>.Width / 2
  expr: Constraints[38] = <<Parameters>>.Depth + <<Parameters>>.Thickness / 2
  sketch-geometry (15):
    g0: LineSegment StartX=-2 StartY=97.5 StartZ=0 EndX=-2 EndY=77.5 EndZ=0
    g1: LineSegment StartX=-2 StartY=77.5 StartZ=0 EndX=-1 EndY=77.5 EndZ=0
    g2: LineSegment StartX=-1 StartY=77.5 StartZ=0 EndX=-1 EndY=97.5 EndZ=0
    g3: LineSegment StartX=-1 StartY=97.5 StartZ=0 EndX=-2 EndY=97.5 EndZ=0
    g4: GeomPoint [constr] X=-1.5 Y=87.5 Z=0
    g5: LineSegment StartX=90 StartY=177 StartZ=0 EndX=90 EndY=176 EndZ=0
    g6: LineSegment StartX=90 StartY=176 StartZ=0 EndX=110 EndY=176 EndZ=0
    g7: LineSegment StartX=110 StartY=176 StartZ=0 EndX=110 EndY=177 EndZ=0
    g8: LineSegment StartX=110 StartY=177 StartZ=0 EndX=90 EndY=177 EndZ=0
    g9: GeomPoint [constr] X=100 Y=176.5 Z=0
    g10: LineSegment StartX=201 StartY=97.5 StartZ=0 EndX=201 EndY=77.5 EndZ=0
    g11: LineSegment StartX=201 StartY=77.5 StartZ=0 EndX=202 EndY=77.5 EndZ=0
    g12: LineSegment StartX=202 StartY=77.5 StartZ=0 EndX=202 EndY=97.5 EndZ=0
    g13: LineSegment StartX=202 StartY=97.5 StartZ=0 EndX=201 EndY=97.5 EndZ=0
    g14: GeomPoint [constr] X=201.5 Y=87.5 Z=0
  constraints (39):
    c: Coincident(g0,g1)
    c: Coincident(g1,g2)
    c: Coincident(g2,g3)
    c: Coincident(g3,g0)
    c: Horizontal(g1)
    c: Horizontal(g3)
    c: Vertical(g0)
    c: Vertical(g2)
    c: Symmetric(g1,g0,g4)
    c: Coincident(g5,g6)
    c: Coincident(g6,g7)
    c: Coincident(g7,g8)
    c: Coincident(g8,g5)
    c: Horizontal(g6)
    c: Horizontal(g8)
    c: Vertical(g5)
    c: Vertical(g7)
    c: Symmetric(g6,g5,g9)
    c: Coincident(g10,g11)
    c: Coincident(g11,g12)
    c: Coincident(g12,g13)
    c: Coincident(g13,g10)
    c: Horizontal(g11)
    c: Horizontal(g13)
    c: Vertical(g10)
    c: Vertical(g12)
    c: Symmetric(g11,g10,g14)
    c: DistanceX(g5,g6) = 20
    c: Equal(g6,g2)
    c: Equal(g6,g10)
    c: DistanceY(g5,g5) = 1
    c: Equal(g5,g3)
    c: Equal(g5,g13)
    c: DistanceX(g1,g-1) = 1
    c: DistanceX(g-1,g10) = 201
    c: DistanceY(g-1,g4) = 87.5
    c: DistanceY(g-1,g14) = 87.5
    c: DistanceX(g-1,g9) = 100
    c: DistanceY(g-1,g5) = 176
FEATURE [PartDesign::Pocket] Pocket011  label="Switch Top Lock Relief"
  AddSubType = 1
  AutoTaperInnerAngle = true
  BaseFeature = -> Pad009
  CheckUpToFaceLimits = true
  ClaimChildren = false
  Fit = 0
  FitJoin = 0
  InnerFit = 0
  InnerFitJoin = 0
  InvalidShape = false
  Length = 19.2
  Length2 = 100
  Linearize = true
  NewSolid = false
  Profile = -> Sketch021
  Suppress = false
  TaperInnerAngle = 0
  TaperInnerAngleRev = 0
  TreeRank = 95
  Type = 0
  ValidateShape = true
  _ProfileBasedVersion = 1
  _Version = 1
  expr: Length = <<Parameters>>.Switch_Top_Height + <<Parameters>>.Thickness
FEATURE [Sketcher::SketchObject] Sketch022  label="Switch Top Air Holes Sketch"
  ArcFitTolerance = 1e-06
  AttachmentSupport = -> [Pocket011]
  ExternalBSplineMaxDegree = 5
  ExternalBSplineTolerance = 0.0001
  FullyConstrained = true
  InternalTolerance = 1e-06
  InvalidShape = false
  MakeInternals = false
  MapMode = 5
  Placement = pos=(0,177,0) rot=(0,0.707107,0.707107;3.14159rad)
  Support = -> [Pocket011]
  TreeRank = 96
  ValidateShape = true
  expr: Constraints[16] = <<Parameters>>.Switch_Air_Hole_Diameter
  expr: Constraints[21] = <<Parameters>>.Switch_Air_Hole_Diameter * 2
  expr: Constraints[43] = <<Parameters>>.Switch_Air_Hole_Diameter * 2
  expr: Constraints[44] = <<Parameters>>.Switch_Air_Hole_Diameter * 2
  expr: Constraints[45] = <<Parameters>>.Switch_Air_Hole_Diameter
  expr: Constraints[46] = <<Parameters>>.Switch_Air_Hole_Diameter * 2
  expr: Constraints[47] = <<Parameters>>.Switch_Bottom_Height + 1.5 * <<Parameters>>.Switch_Air_Hole_Diameter
  expr: Constraints[84] = <<Parameters>>.Switch_Air_Hole_Diameter * 2
  expr: Constraints[85] = <<Parameters>>.Switch_Air_Hole_Diameter * 2
  expr: Constraints[92] = <<Parameters>>.Switch_Air_Hole_Diameter * 2
  expr: Constraints[93] = <<Parameters>>.Switch_Air_Hole_Diameter
  expr: Constraints[94] = <<Parameters>>.Switch_Bottom_Height + 1.5 * <<Parameters>>.Switch_Air_Hole_Diameter
  expr: Constraints[95] = <<Parameters>>.Width - 14 * <<Parameters>>.Switch_Air_Hole_Diameter * 2
  sketch-geometry (32):
    g0: LineSegment StartX=-4.70096 StartY=35.55 StartZ=0 EndX=-6 EndY=37.8 EndZ=0
    g1: LineSegment StartX=-6 StartY=37.8 StartZ=0 EndX=-7.29904 EndY=35.55 EndZ=0
    g2: LineSegment StartX=-7.29904 StartY=35.55 StartZ=0 EndX=-4.70096 EndY=35.55 EndZ=0
    g3: Circle [constr] CenterX=-6 CenterY=36.3 CenterZ=0 NormalX=0 NormalY=0 NormalZ=1 AngleXU=0 Radius=1.5
    g4: LineSegment StartX=-4.70096 StartY=29.55 StartZ=0 EndX=-6 EndY=31.8 EndZ=0
    g5: LineSegment StartX=-6 StartY=31.8 StartZ=0 EndX=-7.29904 EndY=29.55 EndZ=0
    g6: LineSegment StartX=-7.29904 StartY=29.55 StartZ=0 EndX=-4.70096 EndY=29.55 EndZ=0
    g7: Circle [constr] CenterX=-6 CenterY=30.3 CenterZ=0 NormalX=0 NormalY=0 NormalZ=1 AngleXU=0 Radius=1.5
    g8: LineSegment StartX=-10.701 StartY=32.55 StartZ=0 EndX=-12 EndY=34.8 EndZ=0
    g9: LineSegment StartX=-12 StartY=34.8 StartZ=0 EndX=-13.299 EndY=32.55 EndZ=0
    g10: LineSegment StartX=-13.299 StartY=32.55 StartZ=0 EndX=-10.701 EndY=32.55 EndZ=0
    g11: Circle [constr] CenterX=-12 CenterY=33.3 CenterZ=0 NormalX=0 NormalY=0 NormalZ=1 AngleXU=0 Radius=1.5
    g12: LineSegment StartX=-10.701 StartY=26.55 StartZ=0 EndX=-12 EndY=28.8 EndZ=0
    g13: LineSegment StartX=-12 StartY=28.8 StartZ=0 EndX=-13.299 EndY=26.55 EndZ=0
    g14: LineSegment StartX=-13.299 StartY=26.55 StartZ=0 EndX=-10.701 EndY=26.55 EndZ=0
    g15: Circle [constr] CenterX=-12 CenterY=27.3 CenterZ=0 NormalX=0 NormalY=0 NormalZ=1 AngleXU=0 Radius=1.5
    g16: LineSegment StartX=-114.701 StartY=32.55 StartZ=0 EndX=-116 EndY=34.8 EndZ=0
    g17: LineSegment StartX=-116 StartY=34.8 StartZ=0 EndX=-117.299 EndY=32.55 EndZ=0
    g18: LineSegment StartX=-117.299 StartY=32.55 StartZ=0 EndX=-114.701 EndY=32.55 EndZ=0
    g19: Circle [constr] CenterX=-116 CenterY=33.3 CenterZ=0 NormalX=0 NormalY=0 NormalZ=1 AngleXU=0 Radius=1.5
    g20: LineSegment StartX=-114.701 StartY=26.55 StartZ=0 EndX=-116 EndY=28.8 EndZ=0
    g21: LineSegment StartX=-116 StartY=28.8 StartZ=0 EndX=-117.299 EndY=26.55 EndZ=0
    g22: LineSegment StartX=-117.299 StartY=26.55 StartZ=0 EndX=-114.701 EndY=26.55 EndZ=0
    g23: Circle [constr] CenterX=-116 CenterY=27.3 CenterZ=0 NormalX=0 NormalY=0 NormalZ=1 AngleXU=0 Radius=1.5
    g24: LineSegment StartX=-120.701 StartY=29.55 StartZ=0 EndX=-122 EndY=31.8 EndZ=0
    g25: LineSegment StartX=-122 StartY=31.8 StartZ=0 EndX=-123.299 EndY=29.55 EndZ=0
    g26: LineSegment StartX=-123.299 StartY=29.55 StartZ=0 EndX=-120.701 EndY=29.55 EndZ=0
    g27: Circle [constr] CenterX=-122 CenterY=30.3 CenterZ=0 NormalX=0 NormalY=0 NormalZ=1 AngleXU=0 Radius=1.5
    g28: LineSegment StartX=-120.701 StartY=35.55 StartZ=0 EndX=-122 EndY=37.8 EndZ=0
    g29: LineSegment StartX=-122 StartY=37.8 StartZ=0 EndX=-123.299 EndY=35.55 EndZ=0
    g30: LineSegment StartX=-123.299 StartY=35.55 StartZ=0 EndX=-120.701 EndY=35.55 EndZ=0
    g31: Circle [constr] CenterX=-122 CenterY=36.3 CenterZ=0 NormalX=0 NormalY=0 NormalZ=1 AngleXU=0 Radius=1.5
  constraints (96):
    c: Coincident(g0,g1)
    c: Coincident(g1,g2)
    c: Coincident(g2,g0)
    c: Equal(g0,g1)
    c: Equal(g0,g2)
    c: PointOnObject(g0,g3)
    c: PointOnObject(g1,g3)
    c: PointOnObject(g2,g3)
    c: Coincident(g4,g5)
    c: Coincident(g5,g6)
    c: Coincident(g6,g4)
    c: Equal(g4,g5)
    c: Equal(g4,g6)
    c: PointOnObject(g4,g7)
    c: PointOnObject(g5,g7)
    c: PointOnObject(g6,g7)
    c: Diameter(g3) = 3
    c: Equal(g3,g7)
    c: Horizontal(g2)
    c: Horizontal(g6)
    c: DistanceX(g7,g3) = 0
    c: DistanceY(g7,g3) = 6
    c: Coincident(g8,g9)
    c: Coincident(g9,g10)
    c: Coincident(g10,g8)
    c: Equal(g8,g9)
    c: Equal(g8,g10)
    c: PointOnObject(g8,g11)
    c: PointOnObject(g9,g11)
    c: PointOnObject(g10,g11)
    c: Coincident(g12,g13)
    c: Coincident(g13,g14)
    c: Coincident(g14,g12)
    c: Equal(g12,g13)
    c: Equal(g12,g14)
    c: PointOnObject(g12,g15)
    c: PointOnObject(g13,g15)
    c: PointOnObject(g14,g15)
    c: Equal(g3,g11)
    c: Equal(g3,g15)
    c: Horizontal(g10)
    c: Horizontal(g14)
    c: DistanceX(g15,g11) = 0
    c: DistanceY(g15,g11) = 6
    c: DistanceX(g15,g7) = 6
    c: DistanceY(g15,g7) = 3
    c: DistanceX(g7,g-1) = 6
    c: DistanceY(g-1,g15) = 27.3
    c: Coincident(g16,g17)
    c: Coincident(g17,g18)
    c: Coincident(g18,g16)
    c: Equal(g16,g17)
    c: Equal(g16,g18)
    c: PointOnObject(g16,g19)
    c: PointOnObject(g17,g19)
    c: PointOnObject(g18,g19)
    c: Coincident(g20,g21)
    c: Coincident(g21,g22)
    c: Coincident(g22,g20)
    c: Equal(g20,g21)
    c: Equal(g20,g22)
    c: PointOnObject(g20,g23)
    c: PointOnObject(g21,g23)
    c: PointOnObject(g22,g23)
    c: Coincident(g24,g25)
    c: Coincident(g25,g26)
    c: Coincident(g26,g24)
    c: Equal(g24,g25)
    c: Equal(g24,g26)
    c: PointOnObject(g24,g27)
    c: PointOnObject(g25,g27)
    c: PointOnObject(g26,g27)
    c: Coincident(g28,g29)
    c: Coincident(g29,g30)
    c: Coincident(g30,g28)
    c: Equal(g28,g29)
    c: Equal(g28,g30)
    c: PointOnObject(g28,g31)
    c: PointOnObject(g29,g31)
    c: PointOnObject(g30,g31)
    c: Equal(g3,g19)
    c: Equal(g3,g23)
    c: Equal(g3,g27)
    c: Equal(g3,g31)
    c: DistanceY(g23,g19) = 6
    c: DistanceY(g27,g31) = 6
    c: DistanceX(g23,g19) = 0
    c: DistanceX(g31,g27) = 0
    c: Horizontal(g18)
    c: Horizontal(g22)
    c: Horizontal(g26)
    c: Horizontal(g30)
    c: DistanceX(g27,g23) = 6
    c: DistanceY(g23,g27) = 3
    c: DistanceY(g-1,g23) = 27.3
    c: DistanceX(g23,g-1) = 116
FEATURE [PartDesign::Pocket] Pocket012  label="Switch Top Air Holes"
  AddSubType = 1
  AutoTaperInnerAngle = true
  BaseFeature = -> Pocket011
  CheckUpToFaceLimits = true
  ClaimChildren = false
  Fit = 0
  FitJoin = 0
  InnerFit = 0
  InnerFitJoin = 0
  InvalidShape = false
  Length = 2
  Length2 = 100
  Linearize = true
  NewSolid = false
  Profile = -> Sketch022
  Suppress = false
  TaperInnerAngle = 0
  TaperInnerAngleRev = 0
  TreeRank = 97
  Type = 0
  ValidateShape = true
  _ProfileBasedVersion = 1
  _Version = 1
  expr: Length = <<Parameters>>.Thickness
FEATURE [PartDesign::LinearPattern] LinearPattern001  label="Switch Top Air Hole Pattern"
  AddSubType = 0
  BaseFeature = -> Pocket012
  CopyShape = false
  Direction = -> Sketch022 [H_Axis]
  InvalidShape = false
  Length = 72
  NewSolid = false
  Occurrences = 7
  OriginalSubs = -> [Pocket012]
  Originals = -> [Pocket012]
  ParallelTransform = true
  Reversed = true
  SubTransform = true
  Suppress = false
  TreeRank = 98
  ValidateShape = true
  _Version = 3
  expr: Length = <<Parameters>>.Switch_Air_Hole_Diameter * 4 * 6
FEATURE [Sketcher::SketchObject] Sketch023  label="Switch Top Walls Sketch 2"
  ArcFitTolerance = 1e-06
  AttachmentOffset = pos=(0,0,22.8) rot=(0,0,1;0rad)
  AttachmentSupport = -> [XY_Plane003]
  ExternalBSplineMaxDegree = 5
  ExternalBSplineTolerance = 0.0001
  FullyConstrained = true
  InternalTolerance = 1e-06
  InvalidShape = false
  MakeInternals = false
  MapMode = 5
  Placement = pos=(0,0,22.8) rot=(0,0,1;0rad)
  Support = -> [XY_Plane003]
  TreeRank = 88
  ValidateShape = true
  expr: AttachmentOffset.Base.z = <<Parameters>>.Switch_Bottom_Height
  expr: Constraints[10] = <<Parameters>>.Thickness
  expr: Constraints[11] = <<Parameters>>.Thickness
  expr: Constraints[20] = <<Parameters>>.Width
  expr: Constraints[21] = <<Parameters>>.Depth
  expr: Constraints[8] = <<Parameters>>.Width + 2 * <<Parameters>>.Thickness
  expr: Constraints[9] = <<Parameters>>.Depth + 2 * <<Parameters>>.Thickness
  sketch-geometry (8):
    g0: LineSegment StartX=-2 StartY=177 StartZ=0 EndX=202 EndY=177 EndZ=0
    g1: LineSegment StartX=202 StartY=177 StartZ=0 EndX=202 EndY=-2 EndZ=0
    g2: LineSegment StartX=202 StartY=-2 StartZ=0 EndX=-2 EndY=-2 EndZ=0
    g3: LineSegment StartX=-2 StartY=-2 StartZ=0 EndX=-2 EndY=177 EndZ=0
    g4: LineSegment StartX=0 StartY=175 StartZ=0 EndX=200 EndY=175 EndZ=0
    g5: LineSegment StartX=200 StartY=175 StartZ=0 EndX=200 EndY=0 EndZ=0
    g6: LineSegment StartX=200 StartY=0 StartZ=0 EndX=0 EndY=0 EndZ=0
    g7: LineSegment StartX=0 StartY=0 StartZ=0 EndX=0 EndY=175 EndZ=0
  constraints (23):
    c: Coincident(g0,g1)
    c: Coincident(g1,g2)
    c: Coincident(g2,g3)
    c: Coincident(g3,g0)
    c: Horizontal(g0)
    c: Horizontal(g2)
    c: Vertical(g1)
    c: Vertical(g3)
    c: DistanceX(g2,g1) = 204
    c: DistanceY(g2,g0) = 179
    c: DistanceY(g2,g-1) = 2
    c: DistanceX(g2,g-1) = 2
    c: Coincident(g4,g5)
    c: Coincident(g5,g6)
    c: Coincident(g6,g7)
    c: Coincident(g7,g4)
    c: Horizontal(g4)
    c: Horizontal(g6)
    c: Vertical(g5)
    c: Vertical(g7)
    c: DistanceX(g6,g5) = 200
    c: DistanceY(g6,g4) = 175
    c: Coincident(g6,g-1)
FEATURE [PartDesign::Pad] Pad010  label="Switch Top Walls 2"
  AddSubType = 0
  AlongSketchNormal = false
  AutoTaperInnerAngle = true
  CheckUpToFaceLimits = true
  ClaimChildren = false
  Direction = (0,0,1)
  Fit = 0
  FitJoin = 0
  InnerFit = 0
  InnerFitJoin = 0
  InvalidShape = false
  Length = 17.2
  Length2 = 100
  Linearize = true
  NewSolid = false
  Profile = -> Sketch023
  Suppress = false
  TaperInnerAngle = 0
  TaperInnerAngleRev = 0
  TreeRank = 89
  Type = 0
  ValidateShape = true
  _ProfileBasedVersion = 1
  expr: Length = <<Parameters>>.Switch_Top_Height
FEATURE [Sketcher::SketchObject] Sketch025  label="Switch Top Wall Recess Sketch 2"
  ArcFitTolerance = 1e-06
  ExternalBSplineMaxDegree = 5
  ExternalBSplineTolerance = 0.0001
  FullyConstrained = true
  InternalTolerance = 1e-06
  InvalidShape = false
  MakeInternals = false
  MapMode = 5
  Placement = pos=(0,0,22.8) rot=(1,0,0;3.14159rad)
  TreeRank = 92
  ValidateShape = true
  expr: Constraints[10] = <<Parameters>>.Thickness / 2
  expr: Constraints[11] = <<Parameters>>.Thickness / 2
  expr: Constraints[21] = <<Parameters>>.Width
  expr: Constraints[22] = <<Parameters>>.Depth
  expr: Constraints[24] = <<Parameters>>.RJ45_Block_X
  expr: Constraints[26] = <<Parameters>>.RJ45_Block_Width
  expr: Constraints[30] = <<Parameters>>.RJ45_Block_Spacing
  expr: Constraints[34] = <<Parameters>>.RJ45_Block_Width
  expr: Constraints[49] = <<Parameters>>.Switch_LED_Width
  expr: Constraints[50] = <<Parameters>>.Switch_LED_X
  expr: Constraints[8] = <<Parameters>>.Width + <<Parameters>>.Thickness
  expr: Constraints[9] = <<Parameters>>.Depth + <<Parameters>>.Thickness
  sketch-geometry (20):
    g0: LineSegment StartX=-1 StartY=1 StartZ=0 EndX=6.875 EndY=1 EndZ=0
    g1: LineSegment StartX=201 StartY=1 StartZ=0 EndX=201 EndY=-176 EndZ=0
    g2: LineSegment StartX=201 StartY=-176 StartZ=0 EndX=-1 EndY=-176 EndZ=0
    g3: LineSegment StartX=-1 StartY=-176 StartZ=0 EndX=-1 EndY=1 EndZ=0
    g4: LineSegment StartX=0 StartY=0 StartZ=0 EndX=6.875 EndY=0 EndZ=0
    g5: LineSegment StartX=200 StartY=0 StartZ=0 EndX=200 EndY=-175 EndZ=0
    g6: LineSegment StartX=200 StartY=-175 StartZ=0 EndX=0 EndY=-175 EndZ=0
    g7: LineSegment StartX=0 StartY=-175 StartZ=0 EndX=0 EndY=0 EndZ=0
    g8: LineSegment StartX=52.875 StartY=1 StartZ=0 EndX=52.875 EndY=0 EndZ=0
    g9: LineSegment StartX=116.425 StartY=1 StartZ=0 EndX=116.425 EndY=0 EndZ=0
    g10: LineSegment StartX=126.425 StartY=1 StartZ=0 EndX=126.425 EndY=0 EndZ=0
    g11: LineSegment StartX=189.975 StartY=1 StartZ=0 EndX=189.975 EndY=0 EndZ=0
    g12: LineSegment StartX=116.425 StartY=0 StartZ=0 EndX=126.425 EndY=0 EndZ=0
    g13: LineSegment StartX=116.425 StartY=1 StartZ=0 EndX=126.425 EndY=1 EndZ=0
    g14: LineSegment StartX=189.975 StartY=0 StartZ=0 EndX=200 EndY=0 EndZ=0
    g15: LineSegment StartX=189.975 StartY=1 StartZ=0 EndX=201 EndY=1 EndZ=0
    g16: LineSegment StartX=6.875 StartY=1 StartZ=0 EndX=6.875 EndY=0 EndZ=0
    g17: LineSegment StartX=10.775 StartY=1 StartZ=0 EndX=10.775 EndY=0 EndZ=0
    g18: LineSegment StartX=10.775 StartY=0 StartZ=0 EndX=52.875 EndY=0 EndZ=0
    g19: LineSegment StartX=10.775 StartY=1 StartZ=0 EndX=52.875 EndY=1 EndZ=0
  constraints (59):
    c: Coincident(g15,g1)
    c: Coincident(g1,g2)
    c: Coincident(g2,g3)
    c: Coincident(g3,g0)
    c: Horizontal(g0)
    c: Horizontal(g2)
    c: Vertical(g1)
    c: Vertical(g3)
    c: DistanceX(g2,g1) = 202
    c: DistanceY(g1,g15) = 177
    c: DistanceY(g-1,g0) = 1
    c: DistanceX(g0,g-1) = 1
    c: Coincident(g14,g5)
    c: Coincident(g5,g6)
    c: Coincident(g6,g7)
    c: Coincident(g7,g4)
    c: Horizontal(g4)
    c: Horizontal(g6)
    c: Vertical(g5)
    c: Vertical(g7)
    c: Coincident(g4,g-1)
    c: DistanceX(g4,g14) = 200
    c: DistanceY(g6,g4) = 175
    c: Vertical(g8)
    c: DistanceX(g4,g8) = 52.875
    c: Vertical(g9)
    c: DistanceX(g8,g9) = 63.55
    c: PointOnObject(g10,g0)
    c: PointOnObject(g10,g4)
    c: Vertical(g10)
    c: DistanceX(g9,g10) = 10
    c: PointOnObject(g11,g0)
    c: PointOnObject(g11,g4)
    c: Vertical(g11)
    c: DistanceX(g10,g11) = 63.55
    c: Coincident(g18,g8)
    c: Coincident(g12,g9)
    c: Coincident(g19,g8)
    c: Coincident(g13,g9)
    c: Coincident(g13,g10)
    c: Coincident(g12,g10)
    c: Horizontal(g13)
    c: Horizontal(g12)
    c: Horizontal(g15)
    c: Horizontal(g14)
    c: Coincident(g11,g15)
    c: Coincident(g14,g11)
    c: Vertical(g17)
    c: Vertical(g16)
    c: DistanceX(g16,g17) = 3.9
    c: DistanceX(g4,g16) = 6.875
    c: Coincident(g4,g16)
    c: Coincident(g18,g17)
    c: Coincident(g0,g16)
    c: Coincident(g19,g17)
    c: Horizontal(g19)
    c: Horizontal(g18)
    c: PointOnObject(g17,g-1)
    c: Equal(g16,g17)
FEATURE [PartDesign::Pad] Pad012  label="Switch Top Wall Recess 2"
  AddSubType = 0
  AlongSketchNormal = false
  AutoTaperInnerAngle = true
  BaseFeature = -> Pad010
  CheckUpToFaceLimits = true
  ClaimChildren = false
  Direction = (0,0,-1)
  Fit = 0
  FitJoin = 0
  InnerFit = 0
  InnerFitJoin = 0
  InvalidShape = false
  Length = 4
  Length2 = 100
  Linearize = true
  NewSolid = false
  Profile = -> Sketch025
  Suppress = false
  TaperInnerAngle = 0
  TaperInnerAngleRev = 0
  TreeRank = 93
  Type = 0
  ValidateShape = true
  _ProfileBasedVersion = 1
  expr: Length = <<Parameters>>.Thickness * 2
FEATURE [Sketcher::SketchObject] Sketch027  label="Switch Top Air Holes Sketch 2"
  ArcFitTolerance = 1e-06
  ExternalBSplineMaxDegree = 5
  ExternalBSplineTolerance = 0.0001
  FullyConstrained = true
  InternalTolerance = 1e-06
  InvalidShape = false
  MakeInternals = false
  MapMode = 5
  Placement = pos=(0,177,0) rot=(0,0.707107,0.707107;3.14159rad)
  TreeRank = 96
  ValidateShape = true
  expr: Constraints[16] = <<Parameters>>.Switch_Air_Hole_Diameter
  expr: Constraints[19] = <<Parameters>>.Switch_Air_Hole_Diameter * 2
  expr: Constraints[39] = <<Parameters>>.Switch_Air_Hole_Diameter * 2
  expr: Constraints[40] = <<Parameters>>.Switch_Air_Hole_Diameter * 2
  expr: Constraints[41] = <<Parameters>>.Switch_Air_Hole_Diameter
  expr: Constraints[42] = <<Parameters>>.Switch_Air_Hole_Diameter * 2
  expr: Constraints[79] = <<Parameters>>.Switch_Air_Hole_Diameter * 2
  expr: Constraints[80] = <<Parameters>>.Switch_Air_Hole_Diameter * 2
  expr: Constraints[83] = <<Parameters>>.Switch_Air_Hole_Diameter * 2
  expr: Constraints[84] = <<Parameters>>.Switch_Air_Hole_Diameter
  expr: Constraints[85] = <<Parameters>>.Width - 14 * <<Parameters>>.Switch_Air_Hole_Diameter * 2
  expr: Constraints[87] = <<Parameters>>.Switch_Bottom_Height + <<Parameters>>.Switch_Air_Hole_Diameter / 2
  sketch-geometry (32):
    g0: LineSegment StartX=-6 StartY=31.8 StartZ=0 EndX=-4.70096 EndY=34.05 EndZ=0
    g1: LineSegment StartX=-4.70096 StartY=34.05 StartZ=0 EndX=-7.29904 EndY=34.05 EndZ=0
    g2: LineSegment StartX=-7.29904 StartY=34.05 StartZ=0 EndX=-6 EndY=31.8 EndZ=0
    g3: Circle [constr] CenterX=-6 CenterY=33.3 CenterZ=0 NormalX=0 NormalY=0 NormalZ=1 AngleXU=0 Radius=1.5
    g4: LineSegment StartX=-6 StartY=25.8 StartZ=0 EndX=-4.70096 EndY=28.05 EndZ=0
    g5: LineSegment StartX=-4.70096 StartY=28.05 StartZ=0 EndX=-7.29904 EndY=28.05 EndZ=0
    g6: LineSegment StartX=-7.29904 StartY=28.05 StartZ=0 EndX=-6 EndY=25.8 EndZ=0
    g7: Circle [constr] CenterX=-6 CenterY=27.3 CenterZ=0 NormalX=0 NormalY=0 NormalZ=1 AngleXU=0 Radius=1.5
    g8: LineSegment StartX=-12 StartY=28.8 StartZ=0 EndX=-10.701 EndY=31.05 EndZ=0
    g9: LineSegment StartX=-10.701 StartY=31.05 StartZ=0 EndX=-13.299 EndY=31.05 EndZ=0
    g10: LineSegment StartX=-13.299 StartY=31.05 StartZ=0 EndX=-12 EndY=28.8 EndZ=0
    g11: Circle [constr] CenterX=-12 CenterY=30.3 CenterZ=0 NormalX=0 NormalY=0 NormalZ=1 AngleXU=0 Radius=1.5
    g12: LineSegment StartX=-12 StartY=22.8 StartZ=0 EndX=-10.701 EndY=25.05 EndZ=0
    g13: LineSegment StartX=-10.701 StartY=25.05 StartZ=0 EndX=-13.299 EndY=25.05 EndZ=0
    g14: LineSegment StartX=-13.299 StartY=25.05 StartZ=0 EndX=-12 EndY=22.8 EndZ=0
    g15: Circle [constr] CenterX=-12 CenterY=24.3 CenterZ=0 NormalX=0 NormalY=0 NormalZ=1 AngleXU=0 Radius=1.5
    g16: LineSegment StartX=-116 StartY=28.8 StartZ=0 EndX=-114.701 EndY=31.05 EndZ=0
    g17: LineSegment StartX=-114.701 StartY=31.05 StartZ=0 EndX=-117.299 EndY=31.05 EndZ=0
    g18: LineSegment StartX=-117.299 StartY=31.05 StartZ=0 EndX=-116 EndY=28.8 EndZ=0
    g19: Circle [constr] CenterX=-116 CenterY=30.3 CenterZ=0 NormalX=0 NormalY=0 NormalZ=1 AngleXU=0 Radius=1.5
    g20: LineSegment StartX=-114.701 StartY=25.05 StartZ=0 EndX=-117.299 EndY=25.05 EndZ=0
    g21: LineSegment StartX=-117.299 StartY=25.05 StartZ=0 EndX=-116 EndY=22.8 EndZ=0
    g22: LineSegment StartX=-116 StartY=22.8 StartZ=0 EndX=-114.701 EndY=25.05 EndZ=0
    g23: Circle [constr] CenterX=-116 CenterY=24.3 CenterZ=0 NormalX=0 NormalY=0 NormalZ=1 AngleXU=0 Radius=1.5
    g24: LineSegment StartX=-120.701 StartY=28.05 StartZ=0 EndX=-123.299 EndY=28.05 EndZ=0
    g25: LineSegment StartX=-123.299 StartY=28.05 StartZ=0 EndX=-122 EndY=25.8 EndZ=0
    g26: LineSegment StartX=-122 StartY=25.8 StartZ=0 EndX=-120.701 EndY=28.05 EndZ=0
    g27: Circle [constr] CenterX=-122 CenterY=27.3 CenterZ=0 NormalX=0 NormalY=0 NormalZ=1 AngleXU=0 Radius=1.5
    g28: LineSegment StartX=-120.701 StartY=34.05 StartZ=0 EndX=-123.299 EndY=34.05 EndZ=0
    g29: LineSegment StartX=-123.299 StartY=34.05 StartZ=0 EndX=-122 EndY=31.8 EndZ=0
    g30: LineSegment StartX=-122 StartY=31.8 StartZ=0 EndX=-120.701 EndY=34.05 EndZ=0
    g31: Circle [constr] CenterX=-122 CenterY=33.3 CenterZ=0 NormalX=0 NormalY=0 NormalZ=1 AngleXU=0 Radius=1.5
  constraints (96):
    c: Coincident(g0,g1)
    c: Coincident(g1,g2)
    c: Coincident(g2,g0)
    c: Equal(g0,g1)
    c: Equal(g0,g2)
    c: PointOnObject(g0,g3)
    c: PointOnObject(g1,g3)
    c: PointOnObject(g2,g3)
    c: Coincident(g4,g5)
    c: Coincident(g5,g6)
    c: Coincident(g6,g4)
    c: Equal(g4,g5)
    c: Equal(g4,g6)
    c: PointOnObject(g4,g7)
    c: PointOnObject(g5,g7)
    c: PointOnObject(g6,g7)
    c: Diameter(g3) = 3
    c: Equal(g3,g7)
    c: DistanceX(g7,g3) = 0
    c: DistanceY(g7,g3) = 6
    c: Coincident(g8,g9)
    c: Coincident(g9,g10)
    c: Coincident(g10,g8)
    c: Equal(g8,g9)
    c: Equal(g8,g10)
    c: PointOnObject(g8,g11)
    c: PointOnObject(g9,g11)
    c: PointOnObject(g10,g11)
    c: Coincident(g12,g13)
    c: Coincident(g13,g14)
    c: Coincident(g14,g12)
    c: Equal(g12,g13)
    c: Equal(g12,g14)
    c: PointOnObject(g12,g15)
    c: PointOnObject(g13,g15)
    c: PointOnObject(g14,g15)
    c: Equal(g3,g11)
    c: Equal(g3,g15)
    c: DistanceX(g15,g11) = 0
    c: DistanceY(g15,g11) = 6
    c: DistanceX(g15,g7) = 6
    c: DistanceY(g15,g7) = 3
    c: DistanceX(g7,g-1) = 6
    c: Coincident(g16,g17)
    c: Coincident(g17,g18)
    c: Coincident(g18,g16)
    c: Equal(g16,g17)
    c: Equal(g16,g18)
    c: PointOnObject(g16,g19)
    c: PointOnObject(g17,g19)
    c: PointOnObject(g18,g19)
    c: Coincident(g20,g21)
    c: Coincident(g21,g22)
    c: Coincident(g22,g20)
    c: Equal(g20,g21)
    c: Equal(g20,g22)
    c: PointOnObject(g20,g23)
    c: PointOnObject(g21,g23)
    c: PointOnObject(g22,g23)
    c: Coincident(g24,g25)
    c: Coincident(g25,g26)
    c: Coincident(g26,g24)
    c: Equal(g24,g25)
    c: Equal(g24,g26)
    c: PointOnObject(g24,g27)
    c: PointOnObject(g25,g27)
    c: PointOnObject(g26,g27)
    c: Coincident(g28,g29)
    c: Coincident(g29,g30)
    c: Coincident(g30,g28)
    c: Equal(g28,g29)
    c: Equal(g28,g30)
    c: PointOnObject(g28,g31)
    c: PointOnObject(g29,g31)
    c: PointOnObject(g30,g31)
    c: Equal(g3,g19)
    c: Equal(g3,g23)
    c: Equal(g3,g27)
    c: Equal(g3,g31)
    c: DistanceY(g23,g19) = 6
    c: DistanceY(g27,g31) = 6
    c: DistanceX(g23,g19) = 0
    c: DistanceX(g31,g27) = 0
    c: DistanceX(g27,g23) = 6
    c: DistanceY(g23,g27) = 3
    c: DistanceX(g23,g-1) = 116
    c: DistanceY(g23,g15) = 0
    c: DistanceY(g-1,g15) = 24.3
    c: Horizontal(g28)
    c: Horizontal(g17)
    c: Horizontal(g24)
    c: Horizontal(g20)
    c: Horizontal(g9)
    c: Horizontal(g13)
    c: Horizontal(g5)
    c: Horizontal(g1)
FEATURE [PartDesign::Pocket] Pocket014  label="Switch Top Air Holes 2"
  AddSubType = 1
  AutoTaperInnerAngle = true
  BaseFeature = -> Pad012
  CheckUpToFaceLimits = true
  ClaimChildren = false
  Fit = 0
  FitJoin = 0
  InnerFit = 0
  InnerFitJoin = 0
  InvalidShape = false
  Length = 2
  Length2 = 100
  Linearize = true
  NewSolid = false
  Profile = -> Sketch027
  Suppress = false
  TaperInnerAngle = 0
  TaperInnerAngleRev = 0
  TreeRank = 97
  Type = 0
  ValidateShape = true
  _ProfileBasedVersion = 1
  _Version = 1
  expr: Length = <<Parameters>>.Thickness
FEATURE [PartDesign::LinearPattern] LinearPattern002  label="Switch Top Air Hole Pattern 2"
  AddSubType = 0
  BaseFeature = -> Pocket014
  CopyShape = false
  Direction = -> Sketch027 [H_Axis]
  InvalidShape = false
  Length = 72
  NewSolid = false
  Occurrences = 7
  OriginalSubs = -> [Pocket014]
  Originals = -> [Pocket014]
  ParallelTransform = true
  Reversed = true
  SubTransform = true
  Suppress = false
  TreeRank = 98
  ValidateShape = true
  _Version = 3
  expr: Length = <<Parameters>>.Switch_Air_Hole_Diameter * 4 * 6
FEATURE [Sketcher::SketchObject] Sketch028  label="Switch Top Extra Support Sketch"
  ArcFitTolerance = 1e-06
  AttachmentSupport = -> [LinearPattern002]
  ExternalBSplineMaxDegree = 5
  ExternalBSplineTolerance = 0.0001
  FullyConstrained = true
  InternalTolerance = 1e-06
  InvalidShape = false
  MakeInternals = false
  MapMode = 5
  Placement = pos=(0,0,40) rot=(0,0,1;0rad)
  Support = -> [LinearPattern002]
  TreeRank = 100
  ValidateShape = true
  expr: Constraints[19] = <<Parameters>>.Depth
  expr: Constraints[20] = <<Parameters>>.Depth - 4 * <<Parameters>>.Thickness
  expr: Constraints[21] = <<Parameters>>.Width
  expr: Constraints[22] = <<Parameters>>.Width - 4 * <<Parameters>>.Thickness
  sketch-geometry (10):
    g0: LineSegment StartX=1e-16 StartY=175 StartZ=0 EndX=1e-16 EndY=0 EndZ=0
    g1: LineSegment StartX=1e-16 StartY=1e-16 StartZ=0 EndX=200 EndY=1e-16 EndZ=0
    g2: LineSegment StartX=200 StartY=1e-16 StartZ=0 EndX=200 EndY=175 EndZ=0
    g3: LineSegment StartX=200 StartY=175 StartZ=0 EndX=0 EndY=175 EndZ=0
    g4: GeomPoint [constr] X=100 Y=87.5 Z=0
    g5: LineSegment StartX=196 StartY=4 StartZ=0 EndX=196 EndY=171 EndZ=0
    g6: LineSegment StartX=196 StartY=171 StartZ=0 EndX=4 EndY=171 EndZ=0
    g7: LineSegment StartX=4 StartY=171 StartZ=0 EndX=4 EndY=4 EndZ=0
    g8: LineSegment StartX=4 StartY=4 StartZ=0 EndX=196 EndY=4 EndZ=0
    g9: GeomPoint [constr] X=100 Y=87.5 Z=0
  constraints (24):
    c: Coincident(g0,g1)
    c: Coincident(g1,g2)
    c: Coincident(g2,g3)
    c: Coincident(g3,g0)
    c: Horizontal(g1)
    c: Horizontal(g3)
    c: Vertical(g0)
    c: Vertical(g2)
    c: Symmetric(g1,g0,g4)
    c: Coincident(g5,g6)
    c: Coincident(g6,g7)
    c: Coincident(g7,g8)
    c: Coincident(g8,g5)
    c: Horizontal(g6)
    c: Horizontal(g8)
    c: Vertical(g5)
    c: Vertical(g7)
    c: Symmetric(g6,g5,g9)
    c: Coincident(g9,g4)
    c: DistanceY(g2,g2) = 175
    c: DistanceY(g5,g5) = 167
    c: DistanceX(g1,g1) = 200
    c: DistanceX(g8,g8) = 192
    c: Coincident(g0,g-1)
FEATURE [PartDesign::Pad] Pad013  label="Switch Top Extra Support"
  AddSubType = 0
  AlongSketchNormal = false
  AutoTaperInnerAngle = true
  BaseFeature = -> LinearPattern002
  CheckUpToFaceLimits = true
  ClaimChildren = false
  Direction = (0,0,1)
  Fit = 0
  FitJoin = 0
  InnerFit = 0
  InnerFitJoin = 0
  InvalidShape = false
  Length = 4
  Length2 = 100
  Linearize = true
  NewSolid = false
  Profile = -> Sketch028
  Reversed = true
  Suppress = false
  TaperInnerAngle = 0
  TaperInnerAngleRev = 0
  TreeRank = 101
  Type = 0
  ValidateShape = true
  _ProfileBasedVersion = 1
  expr: Length = <<Parameters>>.Thickness * 2
FEATURE [PartDesign::Chamfer] Chamfer  label="Switch Top Support Chamfer"
  AddSubType = 0
  Angle = 45
  Base = -> Pad013 [Edge649,Edge650,Edge652,Edge651]
  BaseFeature = -> Pad013
  ChamferType = 0
  FlipDirection = false
  InvalidShape = false
  NewSolid = false
  Size = 3.9
  Size2 = 1
  SupportTransform = false
  Suppress = false
  TreeRank = 102
  ValidateShape = true
FEATURE [Sketcher::SketchObject] Sketch029  label="Switch Top Lock Relief 2 Sketch"
  ArcFitTolerance = 1e-06
  AttachmentSupport = -> [Chamfer]
  ExternalBSplineMaxDegree = 5
  ExternalBSplineTolerance = 0.0001
  FullyConstrained = true
  InternalTolerance = 1e-06
  InvalidShape = false
  MakeInternals = false
  MapMode = 5
  Placement = pos=(0,0,40) rot=(0,0,1;0rad)
  Support = -> [Chamfer]
  TreeRank = 103
  ValidateShape = true
  expr: Constraints[27] = <<Parameters>>.Locking_Width
  expr: Constraints[28] = <<Parameters>>.Thickness / 2
  expr: Constraints[33] = <<Parameters>>.Depth / 2
  expr: Constraints[34] = <<Parameters>>.Depth / 2
  expr: Constraints[35] = <<Parameters>>.Depth + <<Parameters>>.Thickness
  expr: Constraints[36] = <<Parameters>>.Width + <<Parameters>>.Thickness
  expr: Constraints[37] = <<Parameters>>.Thickness
  expr: Constraints[38] = <<Parameters>>.Width / 2
  sketch-geometry (15):
    g0: LineSegment StartX=-2 StartY=97.5 StartZ=0 EndX=-2 EndY=77.5 EndZ=0
    g1: LineSegment StartX=-2 StartY=77.5 StartZ=0 EndX=-1 EndY=77.5 EndZ=0
    g2: LineSegment StartX=-1 StartY=77.5 StartZ=0 EndX=-1 EndY=97.5 EndZ=0
    g3: LineSegment StartX=-1 StartY=97.5 StartZ=0 EndX=-2 EndY=97.5 EndZ=0
    g4: GeomPoint [constr] X=-1.5 Y=87.5 Z=0
    g5: LineSegment StartX=202 StartY=77.5 StartZ=0 EndX=202 EndY=97.5 EndZ=0
    g6: LineSegment StartX=202 StartY=97.5 StartZ=0 EndX=201 EndY=97.5 EndZ=0
    g7: LineSegment StartX=201 StartY=97.5 StartZ=0 EndX=201 EndY=77.5 EndZ=0
    g8: LineSegment StartX=201 StartY=77.5 StartZ=0 EndX=202 EndY=77.5 EndZ=0
    g9: GeomPoint [constr] X=201.5 Y=87.5 Z=0
    g10: LineSegment StartX=90 StartY=176 StartZ=0 EndX=90 EndY=177 EndZ=0
    g11: LineSegment StartX=90 StartY=177 StartZ=0 EndX=110 EndY=177 EndZ=0
    g12: LineSegment StartX=110 StartY=177 StartZ=0 EndX=110 EndY=176 EndZ=0
    g13: LineSegment StartX=110 StartY=176 StartZ=0 EndX=90 EndY=176 EndZ=0
    g14: GeomPoint [constr] X=100 Y=176.5 Z=0
  constraints (39):
    c: Coincident(g0,g1)
    c: Coincident(g1,g2)
    c: Coincident(g2,g3)
    c: Coincident(g3,g0)
    c: Horizontal(g1)
    c: Horizontal(g3)
    c: Vertical(g0)
    c: Vertical(g2)
    c: Symmetric(g1,g0,g4)
    c: Coincident(g5,g6)
    c: Coincident(g6,g7)
    c: Coincident(g7,g8)
    c: Coincident(g8,g5)
    c: Horizontal(g6)
    c: Horizontal(g8)
    c: Vertical(g5)
    c: Vertical(g7)
    c: Symmetric(g6,g5,g9)
    c: Coincident(g10,g11)
    c: Coincident(g11,g12)
    c: Coincident(g12,g13)
    c: Coincident(g13,g10)
    c: Horizontal(g11)
    c: Horizontal(g13)
    c: Vertical(g10)
    c: Vertical(g12)
    c: Symmetric(g11,g10,g14)
    c: DistanceX(g13,g13) = 20
    c: DistanceY(g12,g12) = 1
    c: Equal(g13,g2)
    c: Equal(g13,g7)
    c: Equal(g12,g6)
    c: Equal(g12,g3)
    c: DistanceY(g-1,g4) = 87.5
    c: DistanceY(g-1,g9) = 87.5
    c: DistanceY(g-1,g10) = 177
    c: DistanceX(g-1,g5) = 202
    c: DistanceX(g0,g-1) = 2
    c: DistanceX(g-1,g14) = 100
FEATURE [PartDesign::Pocket] Pocket015  label="Switch Top Lock Relief 2"
  AddSubType = 1
  AutoTaperInnerAngle = true
  BaseFeature = -> Chamfer
  CheckUpToFaceLimits = true
  ClaimChildren = false
  Fit = 0
  FitJoin = 0
  InnerFit = 0
  InnerFitJoin = 0
  InvalidShape = false
  Length = 17.2
  Length2 = 100
  Linearize = true
  NewSolid = false
  Profile = -> Sketch029
  Suppress = false
  TaperInnerAngle = 0
  TaperInnerAngleRev = 0
  TreeRank = 104
  Type = 0
  ValidateShape = true
  _ProfileBasedVersion = 1
  _Version = 1
  expr: Length = <<Parameters>>.Switch_Top_Height
FEATURE [Sketcher::SketchObject] Sketch030  label="Switch Top RJ45 Holddown 2 Sketch"
  ArcFitTolerance = 1e-06
  AttachmentSupport = -> [Pocket015]
  ExternalBSplineMaxDegree = 5
  ExternalBSplineTolerance = 0.0001
  FullyConstrained = true
  InternalTolerance = 1e-06
  InvalidShape = false
  MakeInternals = false
  MapMode = 5
  Placement = pos=(0,0,22.8) rot=(1,0,0;3.14159rad)
  Support = -> [Pocket015]
  TreeRank = 105
  ValidateShape = true
  expr: Constraints[17] = <<Parameters>>.RJ45_Block_Width
  expr: Constraints[19] = <<Parameters>>.Thickness
  expr: Constraints[22] = <<Parameters>>.RJ45_Block_X
  expr: Constraints[23] = <<Parameters>>.RJ45_Block_Spacing
  sketch-geometry (8):
    g0: LineSegment StartX=52.875 StartY=2 StartZ=0 EndX=116.425 EndY=2 EndZ=0
    g1: LineSegment StartX=116.425 StartY=2 StartZ=0 EndX=116.425 EndY=0 EndZ=0
    g2: LineSegment StartX=116.425 StartY=0 StartZ=0 EndX=52.875 EndY=0 EndZ=0
    g3: LineSegment StartX=52.875 StartY=0 StartZ=0 EndX=52.875 EndY=2 EndZ=0
    g4: LineSegment StartX=126.425 StartY=2 StartZ=0 EndX=189.975 EndY=2 EndZ=0
    g5: LineSegment StartX=189.975 StartY=2 StartZ=0 EndX=189.975 EndY=0 EndZ=0
    g6: LineSegment StartX=189.975 StartY=0 StartZ=0 EndX=126.425 EndY=0 EndZ=0
    g7: LineSegment StartX=126.425 StartY=0 StartZ=0 EndX=126.425 EndY=2 EndZ=0
  constraints (24):
    c: Coincident(g0,g1)
    c: Coincident(g1,g2)
    c: Coincident(g2,g3)
    c: Coincident(g3,g0)
    c: Horizontal(g0)
    c: Horizontal(g2)
    c: Vertical(g1)
    c: Vertical(g3)
    c: PointOnObject(g1,g-1)
    c: Coincident(g4,g5)
    c: Coincident(g5,g6)
    c: Coincident(g6,g7)
    c: Coincident(g7,g4)
    c: Horizontal(g4)
    c: Horizontal(g6)
    c: Vertical(g5)
    c: Vertical(g7)
    c: DistanceX(g0,g0) = 63.55
    c: Equal(g0,g4)
    c: DistanceY(g3,g3) = 2
    c: Equal(g3,g7)
    c: PointOnObject(g6,g-1)
    c: DistanceX(g-1,g2) = 52.875
    c: DistanceX(g1,g6) = 10
FEATURE [PartDesign::Pad] Pad014  label="Switch Top RJ45 Holddown 2"
  AddSubType = 0
  AlongSketchNormal = false
  AutoTaperInnerAngle = true
  BaseFeature = -> Pocket015
  CheckUpToFaceLimits = true
  ClaimChildren = false
  Direction = (0,0,-1)
  Fit = 0
  FitJoin = 0
  InnerFit = 0
  InnerFitJoin = 0
  InvalidShape = false
  Length = 2.55
  Length2 = 100
  Linearize = true
  NewSolid = false
  Profile = -> Sketch030
  Suppress = false
  TaperInnerAngle = 0
  TaperInnerAngleRev = 0
  TreeRank = 106
  Type = 0
  ValidateShape = true
  _ProfileBasedVersion = 1
  expr: Length = <<Parameters>>.Switch_Bottom_Height - <<Parameters>>.RJ45_Block_Y - <<Parameters>>.RJ45_Block_Height
FEATURE [PartDesign::Body] Body003  label="Switch Top 2"
  AutoGroupSolids = false
  ClaimAllChildren = false
  ExportMode = 0
  Group = -> [Sketch023,Pad010,Sketch025,Pad012,Sketch027,Pocket014,LinearPattern002,Sketch028,Pad013,Chamfer,Sketch029,Pocket015,Sketch030,Pad014]
  InvalidShape = false
  Origin = -> Origin003
  Tip = -> Pad014
  TreeRank = 99
  ValidateShape = true
  _ExportChildren = -> [Pad010,Pad012,Pocket014,LinearPattern002,Pad013,Chamfer,Pocket015,Pad014]
  _GroupVersion = 1
FEATURE [Sketcher::SketchObject] Sketch031  label="Switch Top RJ45 Holddown Sketch"
  ArcFitTolerance = 1e-06
  AttachmentSupport = -> [Pocket015]
  ExternalBSplineMaxDegree = 5
  ExternalBSplineTolerance = 0.0001
  FullyConstrained = true
  InternalTolerance = 1e-06
  InvalidShape = false
  MakeInternals = false
  MapMode = 5
  Placement = pos=(0,0,22.8) rot=(1,0,0;3.14159rad)
  Support = -> [Pocket015]
  TreeRank = 107
  ValidateShape = true
  expr: Constraints[17] = <<Parameters>>.RJ45_Block_Width
  expr: Constraints[19] = <<Parameters>>.Thickness
  expr: Constraints[22] = <<Parameters>>.RJ45_Block_X
  expr: Constraints[23] = <<Parameters>>.RJ45_Block_Spacing
  sketch-geometry (8):
    g0: LineSegment StartX=52.875 StartY=2 StartZ=0 EndX=116.425 EndY=2 EndZ=0
    g1: LineSegment StartX=116.425 StartY=2 StartZ=0 EndX=116.425 EndY=0 EndZ=0
    g2: LineSegment StartX=116.425 StartY=0 StartZ=0 EndX=52.875 EndY=0 EndZ=0
    g3: LineSegment StartX=52.875 StartY=0 StartZ=0 EndX=52.875 EndY=2 EndZ=0
    g4: LineSegment StartX=126.425 StartY=2 StartZ=0 EndX=189.975 EndY=2 EndZ=0
    g5: LineSegment StartX=189.975 StartY=2 StartZ=0 EndX=189.975 EndY=0 EndZ=0
    g6: LineSegment StartX=189.975 StartY=0 StartZ=0 EndX=126.425 EndY=0 EndZ=0
    g7: LineSegment StartX=126.425 StartY=0 StartZ=0 EndX=126.425 EndY=2 EndZ=0
  constraints (24):
    c: Coincident(g0,g1)
    c: Coincident(g1,g2)
    c: Coincident(g2,g3)
    c: Coincident(g3,g0)
    c: Horizontal(g0)
    c: Horizontal(g2)
    c: Vertical(g1)
    c: Vertical(g3)
    c: PointOnObject(g1,g-1)
    c: Coincident(g4,g5)
    c: Coincident(g5,g6)
    c: Coincident(g6,g7)
    c: Coincident(g7,g4)
    c: Horizontal(g4)
    c: Horizontal(g6)
    c: Vertical(g5)
    c: Vertical(g7)
    c: DistanceX(g0,g0) = 63.55
    c: Equal(g0,g4)
    c: DistanceY(g3,g3) = 2
    c: Equal(g3,g7)
    c: PointOnObject(g6,g-1)
    c: DistanceX(g-1,g2) = 52.875
    c: DistanceX(g1,g6) = 10
FEATURE [PartDesign::Pad] Pad015  label="Switch Top RJ45 Holddown"
  AddSubType = 0
  AlongSketchNormal = false
  AutoTaperInnerAngle = true
  BaseFeature = -> LinearPattern001
  CheckUpToFaceLimits = true
  ClaimChildren = false
  Direction = (0,0,-1)
  Fit = 0
  FitJoin = 0
  InnerFit = 0
  InnerFitJoin = 0
  InvalidShape = false
  Length = 2.55
  Length2 = 100
  Linearize = true
  NewSolid = false
  Profile = -> Sketch031
  Suppress = false
  TaperInnerAngle = 0
  TaperInnerAngleRev = 0
  TreeRank = 108
  Type = 0
  ValidateShape = true
  _ProfileBasedVersion = 1
  expr: Length = <<Parameters>>.Switch_Bottom_Height - <<Parameters>>.RJ45_Block_Y - <<Parameters>>.RJ45_Block_Height
FEATURE [PartDesign::Body] Body002  label="Switch Top 1"
  AutoGroupSolids = false
  ClaimAllChildren = false
  ExportMode = 0
  Group = -> [Sketch018,Pad007,Sketch019,Pad008,Sketch020,Pad009,Sketch021,Pocket011,Sketch022,Pocket012,LinearPattern001,Sketch031,Pad015]
  InvalidShape = false
  Origin = -> Origin002
  Tip = -> Pad015
  TreeRank = 87
  ValidateShape = true
  _ExportChildren = -> [Pad007,Pad008,Pad009,Pocket011,Pocket012,LinearPattern001,Pad015]
  _GroupVersion = 1
FEATURE [PartDesign::Body] Body  label="Switch Bottom"
  AutoGroupSolids = false
  ClaimAllChildren = false
  ExportMode = 0
  Group = -> [Sketch005,Pad,Sketch006,Pad004,Sketch007,Pocket,Sketch008,Sketch016,Pocket009,Pad005,Sketch009,Pocket001,Sketch011,Pad006,Sketch012,Pocket005,Sketch013,Pocket006,Sketch014,Pocket007,Sketch015,Pocket008,Sketch017,Pocket010,LinearPattern]
  InvalidShape = false
  Origin = -> Origin
  Tip = -> LinearPattern
  TreeRank = 44
  ValidateShape = true
  _ExportChildren = -> [Pad,Pad004,Pocket,Pocket009,Pad005,Pocket001,Pad006,Pocket005,Pocket006,Pocket007,Pocket008,Pocket010,LinearPattern]
  _GroupVersion = 1
FEATURE [PartDesign::Pad] Pad005  label="Walls"
  AddSubType = 0
  AlongSketchNormal = false
  AutoTaperInnerAngle = true
  BaseFeature = -> Pocket009
  CheckUpToFaceLimits = true
  ClaimChildren = false
  Direction = (0,0,1)
  Fit = 0
  FitJoin = 0
  InnerFit = 0
  InnerFitJoin = 0
  InvalidShape = false
  Length = 22.8
  Length2 = 100
  Linearize = true
  NewSolid = false
  Profile = -> Sketch008
  Suppress = false
  TaperInnerAngle = 0
  TaperInnerAngleRev = 0
  TreeRank = 52
  Type = 0
  ValidateShape = true
  _ProfileBasedVersion = 1
  expr: Length = <<Parameters>>.Switch_Bottom_Height
FEATURE [Sketcher::SketchObject] Sketch009  label="Front Holes Sketch"
  ArcFitTolerance = 1e-06
  AttachmentSupport = -> [Pad005]
  ExternalBSplineMaxDegree = 5
  ExternalBSplineTolerance = 0.0001
  FullyConstrained = true
  InternalTolerance = 1e-06
  InvalidShape = false
  MakeInternals = false
  MapMode = 5
  Placement = pos=(0,-2,0) rot=(1,0,0;1.5708rad)
  Support = -> [Pad005]
  TreeRank = 53
  ValidateShape = true
  expr: Constraints[18] = <<Parameters>>.RJ45_Block_Spacing
  expr: Constraints[20] = <<Parameters>>.RJ45_Block_Width
  expr: Constraints[21] = <<Parameters>>.RJ45_Block_Height * 2
  expr: Constraints[22] = <<Parameters>>.RJ45_Block_X
  expr: Constraints[23] = <<Parameters>>.RJ45_Block_Y
  expr: Constraints[24] = <<Parameters>>.Switch_Reset_Diameter
  expr: Constraints[25] = <<Parameters>>.Switch_Reset_X
  expr: Constraints[26] = <<Parameters>>.Switch_Reset_Y
  expr: Constraints[43] = <<Parameters>>.Switch_LED_Width
  expr: Constraints[44] = <<Parameters>>.Switch_LED_Height
  expr: Constraints[47] = <<Parameters>>.Switch_LED_Spacing
  expr: Constraints[49] = <<Parameters>>.Switch_LED_X
  expr: Constraints[50] = <<Parameters>>.Switch_LED_Y
  sketch-geometry (17):
    g0: LineSegment StartX=52.875 StartY=33.5 StartZ=0 EndX=116.425 EndY=33.5 EndZ=0
    g1: LineSegment StartX=116.425 StartY=33.5 StartZ=0 EndX=116.425 EndY=7 EndZ=0
    g2: LineSegment StartX=116.425 StartY=7 StartZ=0 EndX=52.875 EndY=7 EndZ=0
    g3: LineSegment StartX=52.875 StartY=7 StartZ=0 EndX=52.875 EndY=33.5 EndZ=0
    g4: LineSegment StartX=126.425 StartY=33.5 StartZ=0 EndX=189.975 EndY=33.5 EndZ=0
    g5: LineSegment StartX=189.975 StartY=33.5 StartZ=0 EndX=189.975 EndY=7 EndZ=0
    g6: LineSegment StartX=189.975 StartY=7 StartZ=0 EndX=126.425 EndY=7 EndZ=0
    g7: LineSegment StartX=126.425 StartY=7 StartZ=0 EndX=126.425 EndY=33.5 EndZ=0
    g8: Circle CenterX=17.125 CenterY=11 CenterZ=0 NormalX=0 NormalY=0 NormalZ=1 AngleXU=0 Radius=1.875
    g9: LineSegment StartX=6.875 StartY=22.8 StartZ=0 EndX=10.775 EndY=22.8 EndZ=0
    g10: LineSegment StartX=10.775 StartY=22.8 StartZ=0 EndX=10.775 EndY=20.6 EndZ=0
    g11: LineSegment StartX=10.775 StartY=20.6 StartZ=0 EndX=6.875 EndY=20.6 EndZ=0
    g12: LineSegment StartX=6.875 StartY=20.6 StartZ=0 EndX=6.875 EndY=22.8 EndZ=0
    g13: LineSegment StartX=6.875 StartY=16.2 StartZ=0 EndX=10.775 EndY=16.2 EndZ=0
    g14: LineSegment StartX=10.775 StartY=16.2 StartZ=0 EndX=10.775 EndY=14 EndZ=0
    g15: LineSegment StartX=10.775 StartY=14 StartZ=0 EndX=6.875 EndY=14 EndZ=0
    g16: LineSegment StartX=6.875 StartY=14 StartZ=0 EndX=6.875 EndY=16.2 EndZ=0
  constraints (51):
    c: Coincident(g0,g1)
    c: Coincident(g1,g2)
    c: Coincident(g2,g3)
    c: Coincident(g3,g0)
    c: Horizontal(g0)
    c: Horizontal(g2)
    c: Vertical(g1)
    c: Vertical(g3)
    c: Coincident(g4,g5)
    c: Coincident(g5,g6)
    c: Coincident(g6,g7)
    c: Coincident(g7,g4)
    c: Horizontal(g4)
    c: Horizontal(g6)
    c: Vertical(g5)
    c: Vertical(g7)
    c: Equal(g0,g4)
    c: Equal(g1,g7)
    c: DistanceX(g0,g4) = 10
    c: DistanceY(g6,g1) = 0
    c: DistanceX(g0,g0) = 63.55
    c: DistanceY(g2,g0) = 26.5
    c: DistanceX(g-1,g2) = 52.875
    c: DistanceY(g-1,g2) = 7
    c: Diameter(g8) = 3.75
    c: DistanceX(g-1,g8) = 17.125
    c: DistanceY(g-1,g8) = 11
    c: Coincident(g9,g10)
    c: Coincident(g10,g11)
    c: Coincident(g11,g12)
    c: Coincident(g12,g9)
    c: Horizontal(g9)
    c: Horizontal(g11)
    c: Vertical(g10)
    c: Vertical(g12)
    c: Coincident(g13,g14)
    c: Coincident(g14,g15)
    c: Coincident(g15,g16)
    c: Coincident(g16,g13)
    c: Horizontal(g13)
    c: Horizontal(g15)
    c: Vertical(g14)
    c: Vertical(g16)
    c: DistanceX(g9,g9) = 3.9
    c: DistanceY(g10,g9) = 2.2
    c: Equal(g9,g13)
    c: Equal(g10,g14)
    c: DistanceY(g13,g10) = 4.4
    c: DistanceX(g13,g11) = 0
    c: DistanceX(g-1,g15) = 6.875
    c: DistanceY(g-1,g15) = 14
FEATURE [PartDesign::Pocket] Pocket001  label="Front Holes"
  AddSubType = 1
  AutoTaperInnerAngle = true
  BaseFeature = -> Pad005
  CheckUpToFaceLimits = true
  ClaimChildren = false
  Fit = 0
  FitJoin = 0
  InnerFit = 0
  InnerFitJoin = 0
  InvalidShape = false
  Length = 2
  Length2 = 100
  Linearize = true
  NewSolid = false
  Profile = -> Sketch009
  Suppress = false
  TaperInnerAngle = 0
  TaperInnerAngleRev = 0
  TreeRank = 54
  Type = 0
  ValidateShape = true
  _ProfileBasedVersion = 1
  _Version = 1
  expr: Length = <<Parameters>>.Thickness
FEATURE [PartDesign::Pad] Pad006  label="Passthrough Support"
  AddSubType = 0
  AlongSketchNormal = false
  AutoTaperInnerAngle = true
  BaseFeature = -> Pocket001
  CheckUpToFaceLimits = true
  ClaimChildren = false
  Direction = (0,0,1)
  Fit = 0
  FitJoin = 0
  InnerFit = 0
  InnerFitJoin = 0
  InvalidShape = false
  Length = 2
  Length2 = 100
  Linearize = true
  NewSolid = false
  Profile = -> Sketch011
  Suppress = false
  TaperInnerAngle = 0
  TaperInnerAngleRev = 0
  TreeRank = 58
  Type = 0
  ValidateShape = true
  _ProfileBasedVersion = 1
  expr: Length = <<Parameters>>.Thickness
FEATURE [Sketcher::SketchObject] Sketch012  label="Wall Recess Sketch"
  ArcFitTolerance = 1e-06
  AttachmentSupport = -> [Pad006]
  ExternalBSplineMaxDegree = 5
  ExternalBSplineTolerance = 0.0001
  FullyConstrained = true
  InternalTolerance = 1e-06
  InvalidShape = false
  MakeInternals = false
  MapMode = 5
  Placement = pos=(0,0,22.8) rot=(0,0,1;0rad)
  Support = -> [Pad006]
  TreeRank = 64
  ValidateShape = true
  expr: Constraints[10] = <<Parameters>>.Width + <<Parameters>>.Thickness
  expr: Constraints[11] = <<Parameters>>.Depth + <<Parameters>>.Thickness
  expr: Constraints[17] = <<Parameters>>.Switch_LED_Width
  expr: Constraints[18] = <<Parameters>>.Thickness / 2
  expr: Constraints[19] = Spreadsheet.Switch_LED_X
  expr: Constraints[21] = <<Parameters>>.Thickness / 2
  expr: Constraints[8] = <<Parameters>>.Thickness / 2
  expr: Constraints[9] = <<Parameters>>.Thickness / 2
  sketch-geometry (8):
    g0: LineSegment StartX=-1 StartY=176 StartZ=0 EndX=201 EndY=176 EndZ=0
    g1: LineSegment StartX=201 StartY=176 StartZ=0 EndX=201 EndY=-1 EndZ=0
    g2: LineSegment StartX=201 StartY=-1 StartZ=0 EndX=10.775 EndY=-1 EndZ=0
    g3: LineSegment StartX=-1 StartY=-1 StartZ=0 EndX=-1 EndY=176 EndZ=0
    g4: LineSegment StartX=10.775 StartY=-1 StartZ=0 EndX=10.775 EndY=0 EndZ=0
    g5: LineSegment StartX=10.775 StartY=0 StartZ=0 EndX=6.875 EndY=0 EndZ=0
    g6: LineSegment StartX=6.875 StartY=0 StartZ=0 EndX=6.875 EndY=-1 EndZ=0
    g7: LineSegment StartX=6.875 StartY=-1 StartZ=0 EndX=-1 EndY=-1 EndZ=0
  constraints (24):
    c: Coincident(g0,g1)
    c: Coincident(g1,g2)
    c: Coincident(g7,g3)
    c: Coincident(g3,g0)
    c: Horizontal(g0)
    c: Horizontal(g2)
    c: Vertical(g1)
    c: Vertical(g3)
    c: DistanceY(g7,g-1) = 1
    c: DistanceX(g7,g-1) = 1
    c: DistanceX(g7,g1) = 202
    c: DistanceY(g7,g0) = 177
    c: Coincident(g4,g5)
    c: Coincident(g5,g6)
    c: Horizontal(g5)
    c: Vertical(g4)
    c: Vertical(g6)
    c: DistanceX(g6,g4) = 3.9
    c: DistanceY(g4,g4) = 1
    c: DistanceX(g-1,g6) = 6.875
    c: Coincident(g4,g2)
    c: DistanceY(g2,g-1) = 1
    c: Coincident(g7,g6)
    c: Horizontal(g7)
FEATURE [PartDesign::Pocket] Pocket005  label="Wall Recess"
  AddSubType = 1
  AutoTaperInnerAngle = true
  BaseFeature = -> Pad006
  CheckUpToFaceLimits = true
  ClaimChildren = false
  Fit = 0
  FitJoin = 0
  InnerFit = 0
  InnerFitJoin = 0
  InvalidShape = false
  Length = 4
  Length2 = 100
  Linearize = true
  NewSolid = false
  Profile = -> Sketch012
  Suppress = false
  TaperInnerAngle = 0
  TaperInnerAngleRev = 0
  TreeRank = 65
  Type = 0
  ValidateShape = true
  _ProfileBasedVersion = 1
  _Version = 1
  expr: Length = <<Parameters>>.Thickness * 2
FEATURE [Sketcher::SketchObject] Sketch013  label="Lock Relief Sketch"
  ArcFitTolerance = 1e-06
  AttachmentSupport = -> [Pocket005]
  ExternalBSplineMaxDegree = 5
  ExternalBSplineTolerance = 0.0001
  FullyConstrained = true
  InternalTolerance = 1e-06
  InvalidShape = false
  MakeInternals = false
  MapMode = 5
  Placement = pos=(0,0,22.8) rot=(0,0,1;0rad)
  Support = -> [Pocket005]
  TreeRank = 67
  ValidateShape = true
  expr: Constraints[27] = <<Parameters>>.Locking_Width
  expr: Constraints[30] = <<Parameters>>.Thickness * 2
  expr: Constraints[33] = <<Parameters>>.Depth / 2
  expr: Constraints[34] = <<Parameters>>.Depth / 2
  expr: Constraints[35] = <<Parameters>>.Depth + <<Parameters>>.Thickness / 2
  expr: Constraints[36] = <<Parameters>>.Width / 2
  expr: Constraints[37] = <<Parameters>>.Thickness / 2
  expr: Constraints[38] = <<Parameters>>.Width + <<Parameters>>.Thickness / 2
  sketch-geometry (15):
    g0: LineSegment StartX=-5 StartY=97.5 StartZ=0 EndX=-5 EndY=77.5 EndZ=0
    g1: LineSegment StartX=-5 StartY=77.5 StartZ=0 EndX=-1 EndY=77.5 EndZ=0
    g2: LineSegment StartX=-1 StartY=77.5 StartZ=0 EndX=-1 EndY=97.5 EndZ=0
    g3: LineSegment StartX=-1 StartY=97.5 StartZ=0 EndX=-5 EndY=97.5 EndZ=0
    g4: GeomPoint [constr] X=-3 Y=87.5 Z=0
    g5: LineSegment StartX=90 StartY=180 StartZ=0 EndX=90 EndY=176 EndZ=0
    g6: LineSegment StartX=90 StartY=176 StartZ=0 EndX=110 EndY=176 EndZ=0
    g7: LineSegment StartX=110 StartY=176 StartZ=0 EndX=110 EndY=180 EndZ=0
    g8: LineSegment StartX=110 StartY=180 StartZ=0 EndX=90 EndY=180 EndZ=0
    g9: GeomPoint [constr] X=100 Y=178 Z=0
    g10: LineSegment StartX=205 StartY=77.5 StartZ=0 EndX=205 EndY=97.5 EndZ=0
    g11: LineSegment StartX=205 StartY=97.5 StartZ=0 EndX=201 EndY=97.5 EndZ=0
    g12: LineSegment StartX=201 StartY=97.5 StartZ=0 EndX=201 EndY=77.5 EndZ=0
    g13: LineSegment StartX=201 StartY=77.5 StartZ=0 EndX=205 EndY=77.5 EndZ=0
    g14: GeomPoint [constr] X=203 Y=87.5 Z=0
  constraints (39):
    c: Coincident(g0,g1)
    c: Coincident(g1,g2)
    c: Coincident(g2,g3)
    c: Coincident(g3,g0)
    c: Horizontal(g1)
    c: Horizontal(g3)
    c: Vertical(g0)
    c: Vertical(g2)
    c: Symmetric(g1,g0,g4)
    c: Coincident(g5,g6)
    c: Coincident(g6,g7)
    c: Coincident(g7,g8)
    c: Coincident(g8,g5)
    c: Horizontal(g6)
    c: Horizontal(g8)
    c: Vertical(g5)
    c: Vertical(g7)
    c: Symmetric(g6,g5,g9)
    c: Coincident(g10,g11)
    c: Coincident(g11,g12)
    c: Coincident(g12,g13)
    c: Coincident(g13,g10)
    c: Horizontal(g11)
    c: Horizontal(g13)
    c: Vertical(g10)
    c: Vertical(g12)
    c: Symmetric(g11,g10,g14)
    c: DistanceY(g1,g2) = 20
    c: Equal(g2,g6)
    c: Equal(g2,g12)
    c: DistanceX(g0,g1) = 4
    c: Equal(g3,g5)
    c: Equal(g3,g11)
    c: DistanceY(g-1,g4) = 87.5
    c: DistanceY(g-1,g14) = 87.5
    c: DistanceY(g-1,g5) = 176
    c: DistanceX(g-1,g9) = 100
    c: DistanceX(g1,g-1) = 1
    c: DistanceX(g-1,g12) = 201
FEATURE [PartDesign::Pocket] Pocket006  label="Lock Relief"
  AddSubType = 1
  AutoTaperInnerAngle = true
  BaseFeature = -> Pocket005
  CheckUpToFaceLimits = true
  ClaimChildren = false
  Fit = 0
  FitJoin = 0
  InnerFit = 0
  InnerFitJoin = 0
  InvalidShape = false
  Length = 24.8
  Length2 = 100
  Linearize = true
  NewSolid = false
  Profile = -> Sketch013
  Suppress = false
  TaperInnerAngle = 0
  TaperInnerAngleRev = 0
  TreeRank = 68
  Type = 0
  ValidateShape = true
  _ProfileBasedVersion = 1
  _Version = 1
  expr: Length = <<Parameters>>.Switch_Bottom_Height + <<Parameters>>.Thickness
FEATURE [Sketcher::SketchObject] Sketch014  label="Lock Side Bolt Holes Sketch"
  ArcFitTolerance = 1e-06
  AttachmentSupport = -> [Pocket006]
  ExternalBSplineMaxDegree = 5
  ExternalBSplineTolerance = 0.0001
  FullyConstrained = true
  InternalTolerance = 1e-06
  InvalidShape = false
  MakeInternals = false
  MapMode = 5
  Placement = pos=(-1,0,0) rot=(0.57735,-0.57735,-0.57735;2.0944rad)
  Support = -> [Pocket006]
  TreeRank = 69
  ValidateShape = true
  expr: Constraints[0] = <<Parameters>>.Locking_Hole_Offset - <<Parameters>>.Thickness
  expr: Constraints[1] = <<Parameters>>.Locking_Hole_Diameter
  expr: Constraints[2] = <<Parameters>>.Depth / 2
  sketch-geometry (1):
    g0: Circle CenterX=-87.5 CenterY=13 CenterZ=0 NormalX=0 NormalY=0 NormalZ=1 AngleXU=0 Radius=2.75
  constraints (3):
    c: DistanceY(g-1,g0) = 13
    c: Diameter(g0) = 5.5
    c: DistanceX(g0,g-1) = 87.5
FEATURE [PartDesign::Pocket] Pocket007  label="Lock Side Bolt Holes"
  AddSubType = 1
  AutoTaperInnerAngle = true
  BaseFeature = -> Pocket006
  CheckUpToFaceLimits = true
  ClaimChildren = false
  Fit = 0
  FitJoin = 0
  InnerFit = 0
  InnerFitJoin = 0
  InvalidShape = false
  Length = 204
  Length2 = 100
  Linearize = true
  NewSolid = false
  Profile = -> Sketch014
  Suppress = false
  TaperInnerAngle = 0
  TaperInnerAngleRev = 0
  TreeRank = 70
  Type = 0
  ValidateShape = true
  _ProfileBasedVersion = 1
  _Version = 1
  expr: Length = <<Parameters>>.Width + 2 * <<Parameters>>.Thickness
FEATURE [Sketcher::SketchObject] Sketch015  label="Lock Back Bold Hole Sketch"
  ArcFitTolerance = 1e-06
  AttachmentSupport = -> [Pocket007]
  ExternalBSplineMaxDegree = 5
  ExternalBSplineTolerance = 0.0001
  FullyConstrained = true
  InternalTolerance = 1e-06
  InvalidShape = false
  MakeInternals = false
  MapMode = 5
  Placement = pos=(0,176,0) rot=(0,0.707107,0.707107;3.14159rad)
  Support = -> [Pocket007]
  TreeRank = 71
  ValidateShape = true
  expr: Constraints[0] = <<Parameters>>.Locking_Hole_Diameter
  expr: Constraints[1] = <<Parameters>>.Width / 2
  expr: Constraints[2] = <<Parameters>>.Locking_Hole_Offset - <<Parameters>>.Thickness
  sketch-geometry (1):
    g0: Circle CenterX=-100 CenterY=13 CenterZ=0 NormalX=0 NormalY=0 NormalZ=1 AngleXU=0 Radius=2.75
  constraints (3):
    c: Diameter(g0) = 5.5
    c: DistanceX(g0,g-1) = 100
    c: DistanceY(g-1,g0) = 13
FEATURE [PartDesign::Pocket] Pocket008  label="Lock Back Bold Holes"
  AddSubType = 1
  AutoTaperInnerAngle = true
  BaseFeature = -> Pocket007
  CheckUpToFaceLimits = true
  ClaimChildren = false
  Fit = 0
  FitJoin = 0
  InnerFit = 0
  InnerFitJoin = 0
  InvalidShape = false
  Length = 2
  Length2 = 100
  Linearize = true
  NewSolid = false
  Profile = -> Sketch015
  Suppress = false
  TaperInnerAngle = 0
  TaperInnerAngleRev = 0
  TreeRank = 72
  Type = 0
  ValidateShape = true
  _ProfileBasedVersion = 1
  _Version = 1
  expr: Length = <<Parameters>>.Thickness
FEATURE [Sketcher::SketchObject] Sketch016  label="Insert Holes Length"
  ArcFitTolerance = 1e-06
  AttachmentSupport = -> [Pocket008]
  ExternalBSplineMaxDegree = 5
  ExternalBSplineTolerance = 0.0001
  FullyConstrained = true
  InternalTolerance = 1e-06
  InvalidShape = false
  MakeInternals = false
  MapMode = 5
  Placement = pos=(0,0,5.25) rot=(0,0,1;0rad)
  Support = -> [Pocket008]
  TreeRank = 73
  ValidateShape = true
  expr: Constraints[0] = <<Parameters>>.Switch_FR_X
  expr: Constraints[10] = <<Parameters>>.Switch_BL_X
  expr: Constraints[1] = <<Parameters>>.Switch_FR_Y
  expr: Constraints[2] = <<Parameters>>.M3_Insert_Diameter
  expr: Constraints[3] = <<Parameters>>.Switch_BR_X
  expr: Constraints[4] = <<Parameters>>.Switch_BR_Y
  expr: Constraints[5] = <<Parameters>>.Switch_M_Y
  expr: Constraints[6] = <<Parameters>>.Switch_M_X
  expr: Constraints[7] = <<Parameters>>.Switch_FL_X
  expr: Constraints[8] = <<Parameters>>.Switch_FL_Y
  expr: Constraints[9] = <<Parameters>>.Switch_BL_Y
  sketch-geometry (5):
    g0: Circle CenterX=191.375 CenterY=29.5 CenterZ=0 NormalX=0 NormalY=0 NormalZ=1 AngleXU=0 Radius=1.87
    g1: Circle CenterX=8.375 CenterY=43.5 CenterZ=0 NormalX=0 NormalY=0 NormalZ=1 AngleXU=0 Radius=1.87
    g2: Circle CenterX=116.875 CenterY=70 CenterZ=0 NormalX=0 NormalY=0 NormalZ=1 AngleXU=0 Radius=1.87
    g3: Circle CenterX=191.375 CenterY=123 CenterZ=0 NormalX=0 NormalY=0 NormalZ=1 AngleXU=0 Radius=1.87
    g4: Circle CenterX=8.375 CenterY=123 CenterZ=0 NormalX=0 NormalY=0 NormalZ=1 AngleXU=0 Radius=1.87
  constraints (15):
    c: DistanceX(g-1,g0) = 191.375
    c: DistanceY(g-1,g0) = 29.5
    c: Diameter(g0) = 3.74
    c: DistanceX(g-1,g3) = 191.375
    c: DistanceY(g-1,g3) = 123
    c: DistanceY(g-1,g2) = 70
    c: DistanceX(g-1,g2) = 116.875
    c: DistanceX(g-1,g1) = 8.375
    c: DistanceY(g-1,g1) = 43.5
    c: DistanceY(g-1,g4) = 123
    c: DistanceX(g-1,g4) = 8.375
    c: Equal(g0,g2)
    c: Equal(g0,g3)
    c: Equal(g0,g1)
    c: Equal(g0,g4)
FEATURE [PartDesign::Pocket] Pocket009  label="Insert Holes"
  AddSubType = 1
  AutoTaperInnerAngle = true
  BaseFeature = -> Pocket
  CheckUpToFaceLimits = true
  ClaimChildren = false
  Fit = 0
  FitJoin = 0
  InnerFit = 0
  InnerFitJoin = 0
  InvalidShape = false
  Length = 6
  Length2 = 100
  Linearize = true
  NewSolid = false
  Profile = -> Sketch016
  Suppress = false
  TaperInnerAngle = 0
  TaperInnerAngleRev = 0
  TreeRank = 74
  Type = 0
  ValidateShape = true
  _ProfileBasedVersion = 1
  _Version = 1
  expr: Length = <<Parameters>>.Switch_Mount_Type == <<insert>> ? <<Parameters>>.M3_Insert_Length : 0.0001
FEATURE [Sketcher::SketchObject] Sketch017  label="Air Holes Sketch"
  ArcFitTolerance = 1e-06
  AttachmentSupport = -> [Pocket008]
  ExternalBSplineMaxDegree = 5
  ExternalBSplineTolerance = 0.0001
  FullyConstrained = true
  InternalTolerance = 1e-06
  InvalidShape = false
  MakeInternals = false
  MapMode = 5
  Placement = pos=(0,177,0) rot=(0,0.707107,0.707107;3.14159rad)
  Support = -> [Pocket008]
  TreeRank = 75
  ValidateShape = true
  expr: Constraints[109] = <<Parameters>>.Switch_Air_Hole_Diameter * 2
  expr: Constraints[110] = <<Parameters>>.Switch_Air_Hole_Diameter * 2
  expr: Constraints[111] = <<Parameters>>.Switch_Air_Hole_Diameter * 2
  expr: Constraints[115] = <<Parameters>>.Switch_Air_Hole_Diameter * 2
  expr: Constraints[116] = <<Parameters>>.Switch_Air_Hole_Diameter
  expr: Constraints[117] = <<Parameters>>.Switch_Air_Hole_Diameter * 2
  expr: Constraints[118] = <<Parameters>>.Switch_Air_Hole_Diameter * 2
  expr: Constraints[119] = <<Parameters>>.Width - 14 * <<Parameters>>.Switch_Air_Hole_Diameter * 2
  expr: Constraints[30] = <<Parameters>>.Switch_Air_Hole_Diameter * 2
  expr: Constraints[31] = <<Parameters>>.Switch_Air_Hole_Diameter * 2
  expr: Constraints[32] = <<Parameters>>.Switch_Air_Hole_Diameter * 2
  expr: Constraints[33] = <<Parameters>>.Switch_Air_Hole_Diameter * 2
  expr: Constraints[34] = <<Parameters>>.Switch_Air_Hole_Diameter * 2
  expr: Constraints[35] = <<Parameters>>.Switch_Air_Hole_Diameter
  expr: Constraints[56] = <<Parameters>>.Switch_Air_Hole_Diameter * 2
  expr: Constraints[57] = <<Parameters>>.Switch_Air_Hole_Diameter * 2
  expr: Constraints[9] = <<Parameters>>.Switch_Air_Hole_Diameter
  sketch-geometry (40):
    g0: LineSegment StartX=-6 StartY=4.5 StartZ=0 EndX=-7.29904 EndY=2.25 EndZ=0
    g1: LineSegment StartX=-7.29904 StartY=2.25 StartZ=0 EndX=-4.70096 EndY=2.25 EndZ=0
    g2: LineSegment StartX=-4.70096 StartY=2.25 StartZ=0 EndX=-6 EndY=4.5 EndZ=0
    g3: Circle [constr] CenterX=-6 CenterY=3 CenterZ=0 NormalX=0 NormalY=0 NormalZ=1 AngleXU=0 Radius=1.5
    g4: LineSegment StartX=-4.70096 StartY=8.25 StartZ=0 EndX=-6 EndY=10.5 EndZ=0
    g5: LineSegment StartX=-6 StartY=10.5 StartZ=0 EndX=-7.29904 EndY=8.25 EndZ=0
    g6: LineSegment StartX=-7.29904 StartY=8.25 StartZ=0 EndX=-4.70096 EndY=8.25 EndZ=0
    g7: Circle [constr] CenterX=-6 CenterY=9 CenterZ=0 NormalX=0 NormalY=0 NormalZ=1 AngleXU=0 Radius=1.5
    g8: LineSegment StartX=-4.70096 StartY=14.25 StartZ=0 EndX=-6 EndY=16.5 EndZ=0
    g9: LineSegment StartX=-6 StartY=16.5 StartZ=0 EndX=-7.29904 EndY=14.25 EndZ=0
    g10: LineSegment StartX=-7.29904 StartY=14.25 StartZ=0 EndX=-4.70096 EndY=14.25 EndZ=0
    g11: Circle [constr] CenterX=-6 CenterY=15 CenterZ=0 NormalX=0 NormalY=0 NormalZ=1 AngleXU=0 Radius=1.5
    g12: LineSegment StartX=-10.701 StartY=11.25 StartZ=0 EndX=-12 EndY=13.5 EndZ=0
    g13: LineSegment StartX=-12 StartY=13.5 StartZ=0 EndX=-13.299 EndY=11.25 EndZ=0
    g14: LineSegment StartX=-13.299 StartY=11.25 StartZ=0 EndX=-10.701 EndY=11.25 EndZ=0
    g15: Circle [constr] CenterX=-12 CenterY=12 CenterZ=0 NormalX=0 NormalY=0 NormalZ=1 AngleXU=0 Radius=1.5
    g16: LineSegment StartX=-10.701 StartY=5.25 StartZ=0 EndX=-12 EndY=7.5 EndZ=0
    g17: LineSegment StartX=-12 StartY=7.5 StartZ=0 EndX=-13.299 EndY=5.25 EndZ=0
    g18: LineSegment StartX=-13.299 StartY=5.25 StartZ=0 EndX=-10.701 EndY=5.25 EndZ=0
    g19: Circle [constr] CenterX=-12 CenterY=6 CenterZ=0 NormalX=0 NormalY=0 NormalZ=1 AngleXU=0 Radius=1.5
    g20: LineSegment StartX=-114.701 StartY=11.25 StartZ=0 EndX=-116 EndY=13.5 EndZ=0
    g21: LineSegment StartX=-116 StartY=13.5 StartZ=0 EndX=-117.299 EndY=11.25 EndZ=0
    g22: LineSegment StartX=-117.299 StartY=11.25 StartZ=0 EndX=-114.701 EndY=11.25 EndZ=0
    g23: Circle [constr] CenterX=-116 CenterY=12 CenterZ=0 NormalX=0 NormalY=0 NormalZ=1 AngleXU=0 Radius=1.5
    g24: LineSegment StartX=-114.701 StartY=5.25 StartZ=0 EndX=-116 EndY=7.5 EndZ=0
    g25: LineSegment StartX=-116 StartY=7.5 StartZ=0 EndX=-117.299 EndY=5.25 EndZ=0
    g26: LineSegment StartX=-117.299 StartY=5.25 StartZ=0 EndX=-114.701 EndY=5.25 EndZ=0
    g27: Circle [constr] CenterX=-116 CenterY=6 CenterZ=0 NormalX=0 NormalY=0 NormalZ=1 AngleXU=0 Radius=1.5
    g28: LineSegment StartX=-120.701 StartY=14.25 StartZ=0 EndX=-122 EndY=16.5 EndZ=0
    g29: LineSegment StartX=-122 StartY=16.5 StartZ=0 EndX=-123.299 EndY=14.25 EndZ=0
    g30: LineSegment StartX=-123.299 StartY=14.25 StartZ=0 EndX=-120.701 EndY=14.25 EndZ=0
    g31: Circle [constr] CenterX=-122 CenterY=15 CenterZ=0 NormalX=0 NormalY=0 NormalZ=1 AngleXU=0 Radius=1.5
    g32: LineSegment StartX=-120.701 StartY=8.25 StartZ=0 EndX=-122 EndY=10.5 EndZ=0
    g33: LineSegment StartX=-122 StartY=10.5 StartZ=0 EndX=-123.299 EndY=8.25 EndZ=0
    g34: LineSegment StartX=-123.299 StartY=8.25 StartZ=0 EndX=-120.701 EndY=8.25 EndZ=0
    g35: Circle [constr] CenterX=-122 CenterY=9 CenterZ=0 NormalX=0 NormalY=0 NormalZ=1 AngleXU=0 Radius=1.5
    g36: LineSegment StartX=-120.701 StartY=2.25 StartZ=0 EndX=-122 EndY=4.5 EndZ=0
    g37: LineSegment StartX=-122 StartY=4.5 StartZ=0 EndX=-123.299 EndY=2.25 EndZ=0
    g38: LineSegment StartX=-123.299 StartY=2.25 StartZ=0 EndX=-120.701 EndY=2.25 EndZ=0
    g39: Circle [constr] CenterX=-122 CenterY=3 CenterZ=0 NormalX=0 NormalY=0 NormalZ=1 AngleXU=0 Radius=1.5
  constraints (120):
    c: Coincident(g0,g1)
    c: Coincident(g1,g2)
    c: Coincident(g2,g0)
    c: Equal(g0,g1)
    c: Equal(g0,g2)
    c: PointOnObject(g0,g3)
    c: PointOnObject(g1,g3)
    c: PointOnObject(g2,g3)
    c: Horizontal(g1)
    c: Diameter(g3) = 3
    c: Coincident(g4,g5)
    c: Coincident(g5,g6)
    c: Coincident(g6,g4)
    c: Equal(g4,g5)
    c: Equal(g4,g6)
    c: PointOnObject(g4,g7)
    c: PointOnObject(g5,g7)
    c: PointOnObject(g6,g7)
    c: Equal(g3,g7)
    c: Horizontal(g6)
    c: Coincident(g8,g9)
    c: Coincident(g9,g10)
    c: Coincident(g10,g8)
    c: Equal(g8,g9)
    c: Equal(g8,g10)
    c: PointOnObject(g8,g11)
    c: PointOnObject(g9,g11)
    c: PointOnObject(g10,g11)
    c: Equal(g3,g11)
    c: Horizontal(g10)
    c: DistanceX(g3,g-1) = 6
    c: DistanceX(g7,g-1) = 6
    c: DistanceX(g11,g-1) = 6
    c: DistanceY(g3,g7) = 6
    c: DistanceY(g7,g11) = 6
    c: DistanceY(g-1,g3) = 3
    c: Coincident(g12,g13)
    c: Coincident(g13,g14)
    c: Coincident(g14,g12)
    c: Equal(g12,g13)
    c: Equal(g12,g14)
    c: PointOnObject(g12,g15)
    c: PointOnObject(g13,g15)
    c: PointOnObject(g14,g15)
    c: Coincident(g16,g17)
    c: Coincident(g17,g18)
    c: Coincident(g18,g16)
    c: Equal(g16,g17)
    c: Equal(g16,g18)
    c: PointOnObject(g16,g19)
    c: PointOnObject(g17,g19)
    c: PointOnObject(g18,g19)
    c: Equal(g3,g19)
    c: Equal(g3,g15)
    c: Horizontal(g18)
    c: Horizontal(g14)
    c: DistanceY(g19,g15) = 6
    c: DistanceX(g19,g3) = 6
    c: DistanceX(g15,g19) = 0
    c: Coincident(g20,g21)
    c: Coincident(g21,g22)
    c: Coincident(g22,g20)
    c: Equal(g20,g21)
    c: Equal(g20,g22)
    c: PointOnObject(g20,g23)
    c: PointOnObject(g21,g23)
    c: PointOnObject(g22,g23)
    c: Coincident(g24,g25)
    c: Coincident(g25,g26)
    c: Coincident(g26,g24)
    c: Equal(g24,g25)
    c: Equal(g24,g26)
    c: PointOnObject(g24,g27)
    c: PointOnObject(g25,g27)
    c: PointOnObject(g26,g27)
    c: Coincident(g28,g29)
    c: Coincident(g29,g30)
    c: Coincident(g30,g28)
    c: Equal(g28,g29)
    c: Equal(g28,g30)
    c: PointOnObject(g28,g31)
    c: PointOnObject(g29,g31)
    c: PointOnObject(g30,g31)
    c: Coincident(g32,g33)
    c: Coincident(g33,g34)
    c: Coincident(g34,g32)
    c: Equal(g32,g33)
    c: Equal(g32,g34)
    c: PointOnObject(g32,g35)
    c: PointOnObject(g33,g35)
    c: PointOnObject(g34,g35)
    c: Coincident(g36,g37)
    c: Coincident(g37,g38)
    c: Coincident(g38,g36)
    c: Equal(g36,g37)
    c: Equal(g36,g38)
    c: PointOnObject(g36,g39)
    c: PointOnObject(g37,g39)
    c: PointOnObject(g38,g39)
    c: Equal(g3,g27)
    c: Equal(g3,g23)
    c: Equal(g3,g31)
    c: Equal(g3,g35)
    c: Equal(g3,g39)
    c: Horizontal(g26)
    c: Horizontal(g22)
    c: Horizontal(g30)
    c: Horizontal(g34)
    c: Horizontal(g38)
    c: DistanceY(g27,g23) = 6
    c: DistanceY(g39,g35) = 6
    c: DistanceY(g35,g31) = 6
    c: DistanceX(g27,g23) = 0
    c: DistanceX(g39,g35) = 0
    c: DistanceX(g35,g31) = 0
    c: DistanceX(g39,g27) = 6
    c: DistanceY(g-1,g39) = 3
    c: DistanceY(g-1,g27) = 6
    c: DistanceY(g-1,g19) = 6
    c: DistanceX(g27,g-1) = 116
FEATURE [PartDesign::Pocket] Pocket010  label="Air Holes"
  AddSubType = 1
  AutoTaperInnerAngle = true
  BaseFeature = -> Pocket008
  CheckUpToFaceLimits = true
  ClaimChildren = false
  Fit = 0
  FitJoin = 0
  InnerFit = 0
  InnerFitJoin = 0
  InvalidShape = false
  Length = 2
  Length2 = 100
  Linearize = true
  NewSolid = false
  Profile = -> Sketch017
  Suppress = false
  TaperInnerAngle = 0
  TaperInnerAngleRev = 0
  TreeRank = 76
  Type = 0
  ValidateShape = true
  _ProfileBasedVersion = 1
  _Version = 1
  expr: Length = <<Parameters>>.Thickness
FEATURE [PartDesign::LinearPattern] LinearPattern  label="Air Hole Pattern"
  AddSubType = 0
  BaseFeature = -> Pocket010
  CopyShape = false
  Direction = -> Sketch017 [H_Axis]
  InvalidShape = false
  Length = 72
  NewSolid = false
  Occurrences = 7
  OriginalSubs = -> [Pocket010]
  Originals = -> [Pocket010]
  ParallelTransform = true
  Reversed = true
  SubTransform = true
  Suppress = false
  TreeRank = 77
  ValidateShape = true
  _Version = 3
  expr: Length = <<Parameters>>.Switch_Air_Hole_Diameter * 4 * 6
